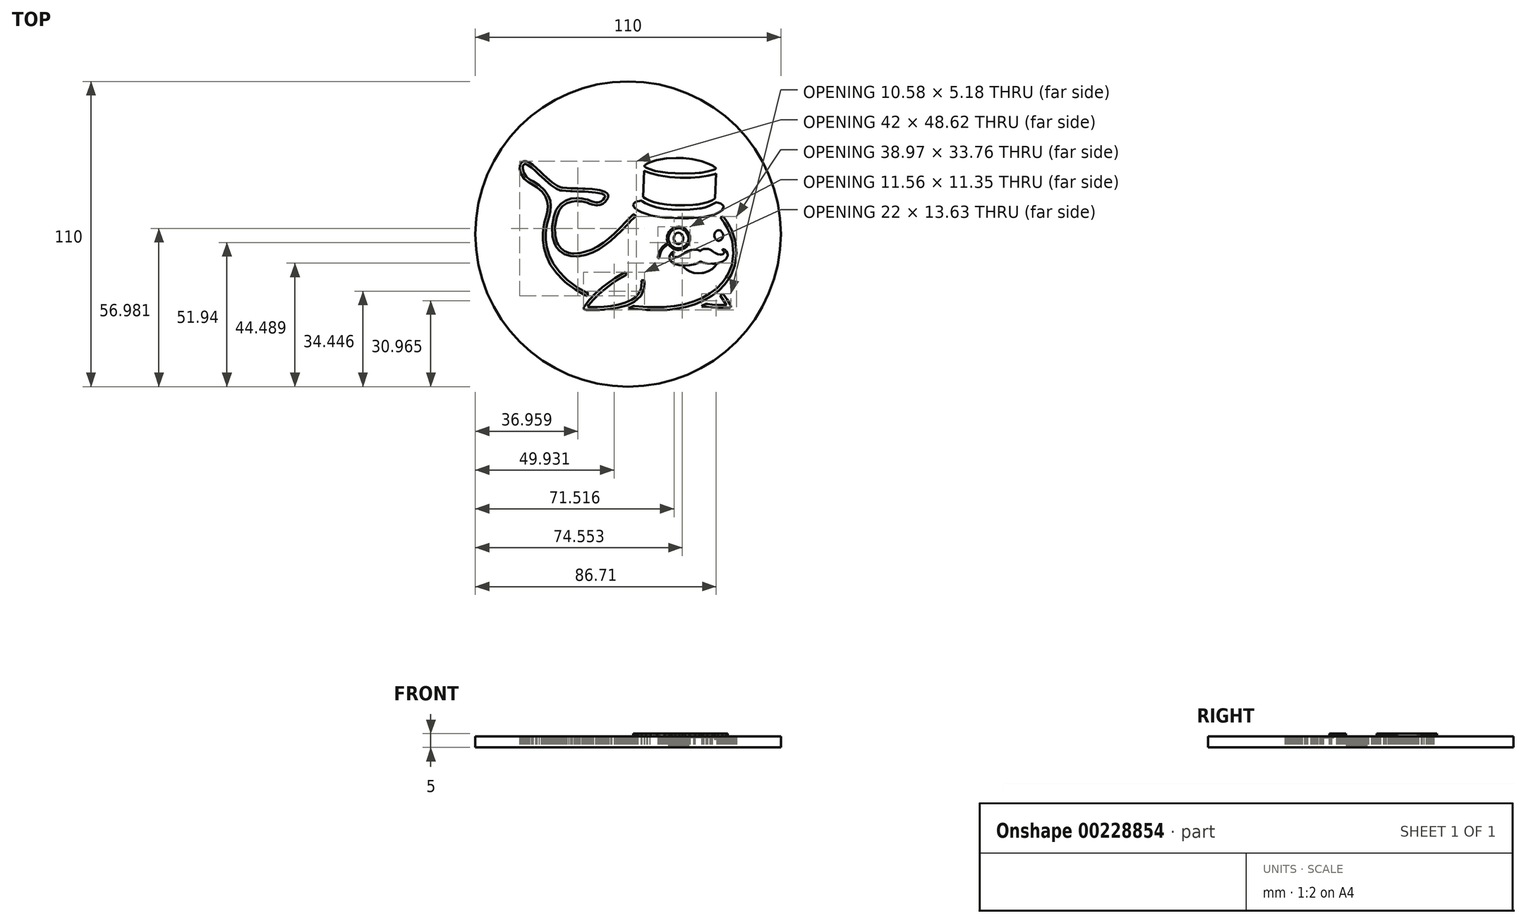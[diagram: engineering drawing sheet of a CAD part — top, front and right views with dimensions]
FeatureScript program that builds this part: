
annotation { "Feature Type Name" : "Feature", "Feature Type Description" : "" }
export const myFeature = defineFeature(function(context is Context, id is Id, definition is map)
    precondition{}
    {
        {
            var Q0;
            Q0=qCreatedBy(makeId("Top.planeOp"),FACE);
            var sketch = newSketch(context, id + "F0", { "sketchPlane" : qUnion([Q0])});
            skLineSegment(sketch, "E0", {"start": v(32.1, -10.6) * mm, "end": v(31.33, -11.62) * mm});
            skLineSegment(sketch, "E1", {"start": v(31.33, -11.62) * mm, "end": v(30.27, -12.6) * mm});
            skLineSegment(sketch, "E2", {"start": v(30.27, -12.6) * mm, "end": v(28.86, -13.41) * mm});
            skLineSegment(sketch, "E3", {"start": v(28.86, -13.41) * mm, "end": v(27.52, -13.88) * mm});
            skLineSegment(sketch, "E4", {"start": v(27.52, -13.88) * mm, "end": v(27.06, -13.97) * mm});
            skLineSegment(sketch, "E5", {"start": v(27.06, -13.97) * mm, "end": v(26.62, -14.05) * mm});
            skLineSegment(sketch, "E6", {"start": v(26.62, -14.05) * mm, "end": v(25.25, -14.14) * mm});
            skLineSegment(sketch, "E7", {"start": v(25.25, -14.14) * mm, "end": v(23.67, -13.98) * mm});
            skLineSegment(sketch, "E8", {"start": v(23.67, -13.98) * mm, "end": v(22.32, -13.55) * mm});
            skLineSegment(sketch, "E9", {"start": v(22.32, -13.55) * mm, "end": v(21.18, -12.9) * mm});
            skLineSegment(sketch, "E10", {"start": v(21.18, -12.9) * mm, "end": v(20.26, -12.09) * mm});
            skLineSegment(sketch, "E11", {"start": v(-13.86, -27.34) * mm, "end": v(-13.89, -27.34) * mm});
            skLineSegment(sketch, "E12", {"start": v(-13.89, -27.34) * mm, "end": v(-14.11, -27.33) * mm});
            skLineSegment(sketch, "E13", {"start": v(-14.11, -27.33) * mm, "end": v(-14.14, -27.33) * mm});
            skLineSegment(sketch, "E14", {"start": v(-14.14, -27.33) * mm, "end": v(-14.36, -27.32) * mm});
            skLineSegment(sketch, "E15", {"start": v(-14.36, -27.32) * mm, "end": v(-15.05, -27.28) * mm});
            skLineSegment(sketch, "E16", {"start": v(-15.05, -27.28) * mm, "end": v(-15.57, -27.22) * mm});
            skLineSegment(sketch, "E17", {"start": v(-15.57, -27.22) * mm, "end": v(-15.82, -27.1) * mm});
            skLineSegment(sketch, "E18", {"start": v(-15.82, -27.1) * mm, "end": v(-15.92, -26.97) * mm});
            skLineSegment(sketch, "E19", {"start": v(-15.92, -26.97) * mm, "end": v(-15.95, -26.92) * mm});
            skLineSegment(sketch, "E20", {"start": v(-15.95, -26.92) * mm, "end": v(-16.07, -26.66) * mm});
            skLineSegment(sketch, "E21", {"start": v(-16.07, -26.66) * mm, "end": v(-15.92, -26.41) * mm});
            skLineSegment(sketch, "E22", {"start": v(-15.92, -26.41) * mm, "end": v(-15.49, -25.72) * mm});
            skLineSegment(sketch, "E23", {"start": v(-15.49, -25.72) * mm, "end": v(-14, -23.78) * mm});
            skLineSegment(sketch, "E24", {"start": v(-14, -23.78) * mm, "end": v(-11.74, -21.38) * mm});
            skLineSegment(sketch, "E25", {"start": v(-11.74, -21.38) * mm, "end": v(-9.33, -19.25) * mm});
            skLineSegment(sketch, "E26", {"start": v(-9.33, -19.25) * mm, "end": v(-6.94, -17.41) * mm});
            skLineSegment(sketch, "E27", {"start": v(-6.94, -17.41) * mm, "end": v(-4.74, -15.91) * mm});
            skLineSegment(sketch, "E28", {"start": v(-4.74, -15.91) * mm, "end": v(-2.9, -14.78) * mm});
            skLineSegment(sketch, "E29", {"start": v(-2.9, -14.78) * mm, "end": v(-1.6, -14.04) * mm});
            skLineSegment(sketch, "E30", {"start": v(-1.6, -14.04) * mm, "end": v(-1.14, -13.8) * mm});
            skLineSegment(sketch, "E31", {"start": v(-1.14, -13.8) * mm, "end": v(-1.03, -13.74) * mm});
            skLineSegment(sketch, "E32", {"start": v(-1.03, -13.74) * mm, "end": v(-0.55, -14.68) * mm});
            skLineSegment(sketch, "E33", {"start": v(-0.55, -14.68) * mm, "end": v(-0.57, -14.7) * mm});
            skLineSegment(sketch, "E34", {"start": v(-0.57, -14.7) * mm, "end": v(-1, -14.92) * mm});
            skLineSegment(sketch, "E35", {"start": v(-1, -14.92) * mm, "end": v(-2.13, -15.57) * mm});
            skLineSegment(sketch, "E36", {"start": v(-2.13, -15.57) * mm, "end": v(-3.81, -16.6) * mm});
            skLineSegment(sketch, "E37", {"start": v(-3.81, -16.6) * mm, "end": v(-5.87, -17.98) * mm});
            skLineSegment(sketch, "E38", {"start": v(-5.87, -17.98) * mm, "end": v(-8.13, -19.67) * mm});
            skLineSegment(sketch, "E39", {"start": v(-8.13, -19.67) * mm, "end": v(-10.44, -21.63) * mm});
            skLineSegment(sketch, "E40", {"start": v(-10.44, -21.63) * mm, "end": v(-12.63, -23.84) * mm});
            skLineSegment(sketch, "E41", {"start": v(-12.63, -23.84) * mm, "end": v(-14.11, -25.62) * mm});
            skLineSegment(sketch, "E42", {"start": v(-14.11, -25.62) * mm, "end": v(-14.54, -26.26) * mm});
            skLineSegment(sketch, "E43", {"start": v(-14.54, -26.26) * mm, "end": v(-14.18, -26.28) * mm});
            skLineSegment(sketch, "E44", {"start": v(-14.18, -26.28) * mm, "end": v(-13.07, -26.3) * mm});
            skLineSegment(sketch, "E45", {"start": v(-13.07, -26.3) * mm, "end": v(-11.07, -26.3) * mm});
            skLineSegment(sketch, "E46", {"start": v(-11.07, -26.3) * mm, "end": v(-8.7, -26.18) * mm});
            skLineSegment(sketch, "E47", {"start": v(-8.7, -26.18) * mm, "end": v(-6.1, -25.9) * mm});
            skLineSegment(sketch, "E48", {"start": v(-6.1, -25.9) * mm, "end": v(-3.47, -25.43) * mm});
            skLineSegment(sketch, "E49", {"start": v(-3.47, -25.43) * mm, "end": v(-0.95, -24.7) * mm});
            skLineSegment(sketch, "E50", {"start": v(-0.95, -24.7) * mm, "end": v(1.31, -23.68) * mm});
            skLineSegment(sketch, "E51", {"start": v(1.31, -23.68) * mm, "end": v(2.74, -22.72) * mm});
            skLineSegment(sketch, "E52", {"start": v(2.74, -22.72) * mm, "end": v(3.14, -22.32) * mm});
            skLineSegment(sketch, "E53", {"start": v(3.14, -22.32) * mm, "end": v(3.51, -21.95) * mm});
            skLineSegment(sketch, "E54", {"start": v(3.51, -21.95) * mm, "end": v(4.66, -19.81) * mm});
            skLineSegment(sketch, "E55", {"start": v(4.66, -19.81) * mm, "end": v(4.85, -17.28) * mm});
            skLineSegment(sketch, "E56", {"start": v(4.85, -17.28) * mm, "end": v(4.75, -16.71) * mm});
            skLineSegment(sketch, "E57", {"start": v(4.75, -16.71) * mm, "end": v(5.8, -16.52) * mm});
            skLineSegment(sketch, "E58", {"start": v(5.8, -16.52) * mm, "end": v(5.93, -17.27) * mm});
            skLineSegment(sketch, "E59", {"start": v(5.93, -17.27) * mm, "end": v(5.8, -19.62) * mm});
            skLineSegment(sketch, "E60", {"start": v(5.8, -19.62) * mm, "end": v(4.6, -22.25) * mm});
            skLineSegment(sketch, "E61", {"start": v(4.6, -22.25) * mm, "end": v(2.24, -24.36) * mm});
            skLineSegment(sketch, "E62", {"start": v(2.24, -24.36) * mm, "end": v(-0.36, -25.65) * mm});
            skLineSegment(sketch, "E63", {"start": v(-0.36, -25.65) * mm, "end": v(-1.27, -25.94) * mm});
            skLineSegment(sketch, "E64", {"start": v(-1.27, -25.94) * mm, "end": v(-1.88, -26.14) * mm});
            skLineSegment(sketch, "E65", {"start": v(-1.88, -26.14) * mm, "end": v(-3.75, -26.58) * mm});
            skLineSegment(sketch, "E66", {"start": v(-3.75, -26.58) * mm, "end": v(-6.24, -27) * mm});
            skLineSegment(sketch, "E67", {"start": v(-6.24, -27) * mm, "end": v(-8.61, -27.24) * mm});
            skLineSegment(sketch, "E68", {"start": v(-8.61, -27.24) * mm, "end": v(-10.17, -27.33) * mm});
            skLineSegment(sketch, "E69", {"start": v(-10.17, -27.33) * mm, "end": v(-10.7, -27.35) * mm});
            skLineSegment(sketch, "E70", {"start": v(-10.7, -27.35) * mm, "end": v(-11.03, -27.36) * mm});
            skLineSegment(sketch, "E71", {"start": v(-11.03, -27.36) * mm, "end": v(-12.5, -27.37) * mm});
            skLineSegment(sketch, "E72", {"start": v(-12.5, -27.37) * mm, "end": v(-13.67, -27.35) * mm});
            skLineSegment(sketch, "E73", {"start": v(-13.67, -27.35) * mm, "end": v(-13.86, -27.34) * mm});
            skLineSegment(sketch, "E74", {"start": v(36.97, -25.78) * mm, "end": v(36.76, -25.4) * mm});
            skLineSegment(sketch, "E75", {"start": v(36.76, -25.4) * mm, "end": v(35.57, -23.58) * mm});
            skLineSegment(sketch, "E76", {"start": v(35.57, -23.58) * mm, "end": v(34.3, -21.79) * mm});
            skLineSegment(sketch, "E77", {"start": v(34.3, -21.79) * mm, "end": v(34.04, -21.45) * mm});
            skLineSegment(sketch, "E78", {"start": v(34.04, -21.45) * mm, "end": v(33.97, -21.5) * mm});
            skLineSegment(sketch, "E79", {"start": v(33.97, -21.5) * mm, "end": v(33.21, -22.11) * mm});
            skLineSegment(sketch, "E80", {"start": v(33.21, -22.11) * mm, "end": v(33.14, -22.17) * mm});
            skLineSegment(sketch, "E81", {"start": v(33.14, -22.17) * mm, "end": v(33.34, -22.44) * mm});
            skLineSegment(sketch, "E82", {"start": v(33.34, -22.44) * mm, "end": v(35.28, -25.25) * mm});
            skLineSegment(sketch, "E83", {"start": v(35.28, -25.25) * mm, "end": v(35.46, -25.54) * mm});
            skLineSegment(sketch, "E84", {"start": v(35.46, -25.54) * mm, "end": v(35.11, -25.55) * mm});
            skLineSegment(sketch, "E85", {"start": v(35.11, -25.55) * mm, "end": v(34.08, -25.57) * mm});
            skLineSegment(sketch, "E86", {"start": v(34.08, -25.57) * mm, "end": v(32.29, -25.53) * mm});
            skLineSegment(sketch, "E87", {"start": v(32.29, -25.53) * mm, "end": v(30.24, -25.4) * mm});
            skLineSegment(sketch, "E88", {"start": v(30.24, -25.4) * mm, "end": v(28.63, -25.22) * mm});
            skLineSegment(sketch, "E89", {"start": v(28.63, -25.22) * mm, "end": v(28.1, -25.13) * mm});
            skLineSegment(sketch, "E90", {"start": v(28.1, -25.13) * mm, "end": v(27.95, -25.2) * mm});
            skLineSegment(sketch, "E91", {"start": v(27.95, -25.2) * mm, "end": v(26.55, -25.84) * mm});
            skLineSegment(sketch, "E92", {"start": v(26.55, -25.84) * mm, "end": v(26.42, -25.9) * mm});
            skLineSegment(sketch, "E93", {"start": v(26.42, -25.9) * mm, "end": v(26.72, -25.96) * mm});
            skLineSegment(sketch, "E94", {"start": v(26.72, -25.96) * mm, "end": v(29.78, -26.42) * mm});
            skLineSegment(sketch, "E95", {"start": v(29.78, -26.42) * mm, "end": v(30.07, -26.45) * mm});
            skLineSegment(sketch, "E96", {"start": v(30.07, -26.45) * mm, "end": v(30.26, -26.47) * mm});
            skLineSegment(sketch, "E97", {"start": v(30.26, -26.47) * mm, "end": v(32.03, -26.58) * mm});
            skLineSegment(sketch, "E98", {"start": v(32.03, -26.58) * mm, "end": v(32.19, -26.59) * mm});
            skLineSegment(sketch, "E99", {"start": v(32.19, -26.59) * mm, "end": v(32.51, -26.6) * mm});
            skLineSegment(sketch, "E100", {"start": v(32.51, -26.6) * mm, "end": v(33.94, -26.62) * mm});
            skLineSegment(sketch, "E101", {"start": v(33.94, -26.62) * mm, "end": v(35.07, -26.61) * mm});
            skLineSegment(sketch, "E102", {"start": v(35.07, -26.61) * mm, "end": v(35.24, -26.6) * mm});
            skLineSegment(sketch, "E103", {"start": v(35.24, -26.6) * mm, "end": v(35.45, -26.6) * mm});
            skLineSegment(sketch, "E104", {"start": v(35.45, -26.6) * mm, "end": v(36.07, -26.58) * mm});
            skLineSegment(sketch, "E105", {"start": v(36.07, -26.58) * mm, "end": v(36.55, -26.53) * mm});
            skLineSegment(sketch, "E106", {"start": v(36.55, -26.53) * mm, "end": v(36.81, -26.44) * mm});
            skLineSegment(sketch, "E107", {"start": v(36.81, -26.44) * mm, "end": v(36.93, -26.33) * mm});
            skLineSegment(sketch, "E108", {"start": v(36.93, -26.33) * mm, "end": v(36.96, -26.28) * mm});
            skLineSegment(sketch, "E109", {"start": v(36.96, -26.28) * mm, "end": v(36.99, -26.24) * mm});
            skLineSegment(sketch, "E110", {"start": v(36.99, -26.24) * mm, "end": v(37, -25.82) * mm});
            skLineSegment(sketch, "E111", {"start": v(37, -25.82) * mm, "end": v(36.97, -25.78) * mm});
            skLineSegment(sketch, "E112", {"start": v(2.96, 6.57) * mm, "end": v(2.86, 6.61) * mm});
            skLineSegment(sketch, "E113", {"start": v(2.86, 6.61) * mm, "end": v(1.97, 7.02) * mm});
            skLineSegment(sketch, "E114", {"start": v(1.97, 7.02) * mm, "end": v(1.89, 7.06) * mm});
            skLineSegment(sketch, "E115", {"start": v(1.89, 7.06) * mm, "end": v(1.65, 6.85) * mm});
            skLineSegment(sketch, "E116", {"start": v(1.65, 6.85) * mm, "end": v(0.96, 6.21) * mm});
            skLineSegment(sketch, "E117", {"start": v(0.96, 6.21) * mm, "end": v(0.2, 5.45) * mm});
            skLineSegment(sketch, "E118", {"start": v(0.2, 5.45) * mm, "end": v(-0.57, 4.63) * mm});
            skLineSegment(sketch, "E119", {"start": v(-0.57, 4.63) * mm, "end": v(-1.3, 3.87) * mm});
            skLineSegment(sketch, "E120", {"start": v(-1.3, 3.87) * mm, "end": v(-1.53, 3.62) * mm});
            skLineSegment(sketch, "E121", {"start": v(-1.53, 3.62) * mm, "end": v(-1.95, 3.19) * mm});
            skLineSegment(sketch, "E122", {"start": v(-1.95, 3.19) * mm, "end": v(-3.23, 1.88) * mm});
            skLineSegment(sketch, "E123", {"start": v(-3.23, 1.88) * mm, "end": v(-5, 0.14) * mm});
            skLineSegment(sketch, "E124", {"start": v(-5, 0.14) * mm, "end": v(-6.86, -1.54) * mm});
            skLineSegment(sketch, "E125", {"start": v(-6.86, -1.54) * mm, "end": v(-8.83, -3.1) * mm});
            skLineSegment(sketch, "E126", {"start": v(-8.83, -3.1) * mm, "end": v(-10.92, -4.48) * mm});
            skLineSegment(sketch, "E127", {"start": v(-10.92, -4.48) * mm, "end": v(-13.15, -5.62) * mm});
            skLineSegment(sketch, "E128", {"start": v(-13.15, -5.62) * mm, "end": v(-15.54, -6.45) * mm});
            skLineSegment(sketch, "E129", {"start": v(-15.54, -6.45) * mm, "end": v(-17.46, -6.86) * mm});
            skLineSegment(sketch, "E130", {"start": v(-17.46, -6.86) * mm, "end": v(-18.1, -6.93) * mm});
            skLineSegment(sketch, "E131", {"start": v(-18.1, -6.93) * mm, "end": v(-18.24, -6.94) * mm});
            skLineSegment(sketch, "E132", {"start": v(-18.24, -6.94) * mm, "end": v(-19.5, -6.99) * mm});
            skLineSegment(sketch, "E133", {"start": v(-19.5, -6.99) * mm, "end": v(-19.62, -6.98) * mm});
            skLineSegment(sketch, "E134", {"start": v(-19.62, -6.98) * mm, "end": v(-20.07, -6.97) * mm});
            skLineSegment(sketch, "E135", {"start": v(-20.07, -6.97) * mm, "end": v(-21.4, -6.72) * mm});
            skLineSegment(sketch, "E136", {"start": v(-21.4, -6.72) * mm, "end": v(-22.93, -6.1) * mm});
            skLineSegment(sketch, "E137", {"start": v(-22.93, -6.1) * mm, "end": v(-24.19, -5.1) * mm});
            skLineSegment(sketch, "E138", {"start": v(-24.19, -5.1) * mm, "end": v(-24.98, -4.1) * mm});
            skLineSegment(sketch, "E139", {"start": v(-24.98, -4.1) * mm, "end": v(-25.18, -3.73) * mm});
            skLineSegment(sketch, "E140", {"start": v(-25.18, -3.73) * mm, "end": v(-25.55, -3.05) * mm});
            skLineSegment(sketch, "E141", {"start": v(-25.55, -3.05) * mm, "end": v(-26.17, -0.73) * mm});
            skLineSegment(sketch, "E142", {"start": v(-26.17, -0.73) * mm, "end": v(-26.31, 2.66) * mm});
            skLineSegment(sketch, "E143", {"start": v(-26.31, 2.66) * mm, "end": v(-25.74, 5.98) * mm});
            skLineSegment(sketch, "E144", {"start": v(-25.74, 5.98) * mm, "end": v(-24.97, 8.14) * mm});
            skLineSegment(sketch, "E145", {"start": v(-24.97, 8.14) * mm, "end": v(-24.6, 8.79) * mm});
            skLineSegment(sketch, "E146", {"start": v(-24.6, 8.79) * mm, "end": v(-24.37, 9.17) * mm});
            skLineSegment(sketch, "E147", {"start": v(-24.37, 9.17) * mm, "end": v(-23.49, 10.18) * mm});
            skLineSegment(sketch, "E148", {"start": v(-23.49, 10.18) * mm, "end": v(-22.03, 11.15) * mm});
            skLineSegment(sketch, "E149", {"start": v(-22.03, 11.15) * mm, "end": v(-20.22, 11.7) * mm});
            skLineSegment(sketch, "E150", {"start": v(-20.22, 11.7) * mm, "end": v(-18.6, 11.85) * mm});
            skLineSegment(sketch, "E151", {"start": v(-18.6, 11.85) * mm, "end": v(-18.07, 11.83) * mm});
            skLineSegment(sketch, "E152", {"start": v(-18.07, 11.83) * mm, "end": v(-17.73, 11.82) * mm});
            skLineSegment(sketch, "E153", {"start": v(-17.73, 11.82) * mm, "end": v(-16.72, 11.7) * mm});
            skLineSegment(sketch, "E154", {"start": v(-16.72, 11.7) * mm, "end": v(-15.61, 11.51) * mm});
            skLineSegment(sketch, "E155", {"start": v(-15.61, 11.51) * mm, "end": v(-14.87, 11.33) * mm});
            skLineSegment(sketch, "E156", {"start": v(-14.87, 11.33) * mm, "end": v(-14.66, 11.24) * mm});
            skLineSegment(sketch, "E157", {"start": v(-14.66, 11.24) * mm, "end": v(-14.6, 11.24) * mm});
            skLineSegment(sketch, "E158", {"start": v(-14.6, 11.24) * mm, "end": v(-14.33, 11.15) * mm});
            skLineSegment(sketch, "E159", {"start": v(-14.33, 11.15) * mm, "end": v(-14.1, 11.06) * mm});
            skLineSegment(sketch, "E160", {"start": v(-14.1, 11.06) * mm, "end": v(-12.86, 10.63) * mm});
            skLineSegment(sketch, "E161", {"start": v(-12.86, 10.63) * mm, "end": v(-11.55, 10.36) * mm});
            skLineSegment(sketch, "E162", {"start": v(-11.55, 10.36) * mm, "end": v(-11.28, 10.35) * mm});
            skLineSegment(sketch, "E163", {"start": v(-11.28, 10.35) * mm, "end": v(-11, 10.34) * mm});
            skLineSegment(sketch, "E164", {"start": v(-11, 10.34) * mm, "end": v(-10.15, 10.46) * mm});
            skLineSegment(sketch, "E165", {"start": v(-10.15, 10.46) * mm, "end": v(-9.14, 10.88) * mm});
            skLineSegment(sketch, "E166", {"start": v(-9.14, 10.88) * mm, "end": v(-8.25, 11.6) * mm});
            skLineSegment(sketch, "E167", {"start": v(-8.25, 11.6) * mm, "end": v(-7.64, 12.38) * mm});
            skLineSegment(sketch, "E168", {"start": v(-7.64, 12.38) * mm, "end": v(-7.47, 12.66) * mm});
            skLineSegment(sketch, "E169", {"start": v(-7.47, 12.66) * mm, "end": v(-7.4, 12.78) * mm});
            skLineSegment(sketch, "E170", {"start": v(-7.4, 12.78) * mm, "end": v(-7.23, 13.2) * mm});
            skLineSegment(sketch, "E171", {"start": v(-7.23, 13.2) * mm, "end": v(-7.16, 13.67) * mm});
            skLineSegment(sketch, "E172", {"start": v(-7.16, 13.67) * mm, "end": v(-7.21, 14.05) * mm});
            skLineSegment(sketch, "E173", {"start": v(-7.21, 14.05) * mm, "end": v(-7.3, 14.29) * mm});
            skLineSegment(sketch, "E174", {"start": v(-7.3, 14.29) * mm, "end": v(-7.33, 14.36) * mm});
            skLineSegment(sketch, "E175", {"start": v(-7.33, 14.36) * mm, "end": v(-7.49, 14.64) * mm});
            skLineSegment(sketch, "E176", {"start": v(-7.49, 14.64) * mm, "end": v(-8.36, 15.25) * mm});
            skLineSegment(sketch, "E177", {"start": v(-8.36, 15.25) * mm, "end": v(-10.22, 15.82) * mm});
            skLineSegment(sketch, "E178", {"start": v(-10.22, 15.82) * mm, "end": v(-12.86, 16.17) * mm});
            skLineSegment(sketch, "E179", {"start": v(-12.86, 16.17) * mm, "end": v(-15.36, 16.32) * mm});
            skLineSegment(sketch, "E180", {"start": v(-15.36, 16.32) * mm, "end": v(-16.2, 16.35) * mm});
            skLineSegment(sketch, "E181", {"start": v(-16.2, 16.35) * mm, "end": v(-16.38, 16.36) * mm});
            skLineSegment(sketch, "E182", {"start": v(-16.38, 16.36) * mm, "end": v(-18.12, 16.42) * mm});
            skLineSegment(sketch, "E183", {"start": v(-18.12, 16.42) * mm, "end": v(-18.29, 16.42) * mm});
            skLineSegment(sketch, "E184", {"start": v(-18.29, 16.42) * mm, "end": v(-18.45, 16.43) * mm});
            skLineSegment(sketch, "E185", {"start": v(-18.45, 16.43) * mm, "end": v(-20.07, 16.48) * mm});
            skLineSegment(sketch, "E186", {"start": v(-20.07, 16.48) * mm, "end": v(-20.22, 16.48) * mm});
            skLineSegment(sketch, "E187", {"start": v(-20.22, 16.48) * mm, "end": v(-20.5, 16.5) * mm});
            skLineSegment(sketch, "E188", {"start": v(-20.5, 16.5) * mm, "end": v(-22.06, 16.57) * mm});
            skLineSegment(sketch, "E189", {"start": v(-22.06, 16.57) * mm, "end": v(-23.57, 16.7) * mm});
            skLineSegment(sketch, "E190", {"start": v(-23.57, 16.7) * mm, "end": v(-23.82, 16.74) * mm});
            skLineSegment(sketch, "E191", {"start": v(-23.82, 16.74) * mm, "end": v(-24.25, 16.8) * mm});
            skLineSegment(sketch, "E192", {"start": v(-24.25, 16.8) * mm, "end": v(-25.5, 17.35) * mm});
            skLineSegment(sketch, "E193", {"start": v(-25.5, 17.35) * mm, "end": v(-27.32, 18.6) * mm});
            skLineSegment(sketch, "E194", {"start": v(-27.32, 18.6) * mm, "end": v(-29.21, 20.23) * mm});
            skLineSegment(sketch, "E195", {"start": v(-29.21, 20.23) * mm, "end": v(-30.62, 21.55) * mm});
            skLineSegment(sketch, "E196", {"start": v(-30.62, 21.55) * mm, "end": v(-31.08, 22) * mm});
            skLineSegment(sketch, "E197", {"start": v(-31.08, 22) * mm, "end": v(-31.5, 22.4) * mm});
            skLineSegment(sketch, "E198", {"start": v(-31.5, 22.4) * mm, "end": v(-32.8, 23.61) * mm});
            skLineSegment(sketch, "E199", {"start": v(-32.8, 23.61) * mm, "end": v(-34.38, 24.97) * mm});
            skLineSegment(sketch, "E200", {"start": v(-34.38, 24.97) * mm, "end": v(-35.8, 25.91) * mm});
            skLineSegment(sketch, "E201", {"start": v(-35.8, 25.91) * mm, "end": v(-36.74, 26.28) * mm});
            skLineSegment(sketch, "E202", {"start": v(-36.74, 26.28) * mm, "end": v(-37.06, 26.29) * mm});
            skLineSegment(sketch, "E203", {"start": v(-37.06, 26.29) * mm, "end": v(-37.16, 26.3) * mm});
            skLineSegment(sketch, "E204", {"start": v(-37.16, 26.3) * mm, "end": v(-37.48, 26.25) * mm});
            skLineSegment(sketch, "E205", {"start": v(-37.48, 26.25) * mm, "end": v(-37.94, 26.08) * mm});
            skLineSegment(sketch, "E206", {"start": v(-37.94, 26.08) * mm, "end": v(-38.38, 25.73) * mm});
            skLineSegment(sketch, "E207", {"start": v(-38.38, 25.73) * mm, "end": v(-38.69, 25.28) * mm});
            skLineSegment(sketch, "E208", {"start": v(-38.69, 25.28) * mm, "end": v(-38.76, 25.12) * mm});
            skLineSegment(sketch, "E209", {"start": v(-38.76, 25.12) * mm, "end": v(-38.92, 24.76) * mm});
            skLineSegment(sketch, "E210", {"start": v(-38.92, 24.76) * mm, "end": v(-39.04, 23.5) * mm});
            skLineSegment(sketch, "E211", {"start": v(-39.04, 23.5) * mm, "end": v(-38.6, 21.7) * mm});
            skLineSegment(sketch, "E212", {"start": v(-38.6, 21.7) * mm, "end": v(-37.42, 19.93) * mm});
            skLineSegment(sketch, "E213", {"start": v(-37.42, 19.93) * mm, "end": v(-36.04, 18.76) * mm});
            skLineSegment(sketch, "E214", {"start": v(-36.04, 18.76) * mm, "end": v(-35.52, 18.48) * mm});
            skLineSegment(sketch, "E215", {"start": v(-35.52, 18.48) * mm, "end": v(-34.83, 18.1) * mm});
            skLineSegment(sketch, "E216", {"start": v(-34.83, 18.1) * mm, "end": v(-32.85, 16.81) * mm});
            skLineSegment(sketch, "E217", {"start": v(-32.85, 16.81) * mm, "end": v(-30.96, 15.15) * mm});
            skLineSegment(sketch, "E218", {"start": v(-30.96, 15.15) * mm, "end": v(-29.75, 13.49) * mm});
            skLineSegment(sketch, "E219", {"start": v(-29.75, 13.49) * mm, "end": v(-29.1, 11.81) * mm});
            skLineSegment(sketch, "E220", {"start": v(-29.1, 11.81) * mm, "end": v(-28.88, 10.14) * mm});
            skLineSegment(sketch, "E221", {"start": v(-28.88, 10.14) * mm, "end": v(-29.02, 8.44) * mm});
            skLineSegment(sketch, "E222", {"start": v(-29.02, 8.44) * mm, "end": v(-29.38, 6.73) * mm});
            skLineSegment(sketch, "E223", {"start": v(-29.38, 6.73) * mm, "end": v(-29.73, 5.44) * mm});
            skLineSegment(sketch, "E224", {"start": v(-29.73, 5.44) * mm, "end": v(-29.85, 5) * mm});
            skLineSegment(sketch, "E225", {"start": v(-29.85, 5) * mm, "end": v(-29.98, 4.58) * mm});
            skLineSegment(sketch, "E226", {"start": v(-29.98, 4.58) * mm, "end": v(-30.11, 4.1) * mm});
            skLineSegment(sketch, "E227", {"start": v(-30.11, 4.1) * mm, "end": v(-30.43, 2.65) * mm});
            skLineSegment(sketch, "E228", {"start": v(-30.43, 2.65) * mm, "end": v(-30.71, 0.37) * mm});
            skLineSegment(sketch, "E229", {"start": v(-30.71, 0.37) * mm, "end": v(-30.72, -2.2) * mm});
            skLineSegment(sketch, "E230", {"start": v(-30.72, -2.2) * mm, "end": v(-30.34, -5) * mm});
            skLineSegment(sketch, "E231", {"start": v(-30.34, -5) * mm, "end": v(-29.46, -7.96) * mm});
            skLineSegment(sketch, "E232", {"start": v(-29.46, -7.96) * mm, "end": v(-27.95, -11.04) * mm});
            skLineSegment(sketch, "E233", {"start": v(-27.95, -11.04) * mm, "end": v(-25.7, -14.17) * mm});
            skLineSegment(sketch, "E234", {"start": v(-25.7, -14.17) * mm, "end": v(-23.44, -16.57) * mm});
            skLineSegment(sketch, "E235", {"start": v(-23.44, -16.57) * mm, "end": v(-22.62, -17.3) * mm});
            skLineSegment(sketch, "E236", {"start": v(-22.62, -17.3) * mm, "end": v(-22.06, -17.78) * mm});
            skLineSegment(sketch, "E237", {"start": v(-22.06, -17.78) * mm, "end": v(-19, -20) * mm});
            skLineSegment(sketch, "E238", {"start": v(-19, -20) * mm, "end": v(-15.6, -21.98) * mm});
            skLineSegment(sketch, "E239", {"start": v(-15.6, -21.98) * mm, "end": v(-14.86, -22.33) * mm});
            skLineSegment(sketch, "E240", {"start": v(-14.86, -22.33) * mm, "end": v(-14.81, -22.26) * mm});
            skLineSegment(sketch, "E241", {"start": v(-14.81, -22.26) * mm, "end": v(-14.3, -21.53) * mm});
            skLineSegment(sketch, "E242", {"start": v(-14.3, -21.53) * mm, "end": v(-14.23, -21.45) * mm});
            skLineSegment(sketch, "E243", {"start": v(-14.23, -21.45) * mm, "end": v(-14.96, -21.1) * mm});
            skLineSegment(sketch, "E244", {"start": v(-14.96, -21.1) * mm, "end": v(-18.34, -19.17) * mm});
            skLineSegment(sketch, "E245", {"start": v(-18.34, -19.17) * mm, "end": v(-21.37, -16.97) * mm});
            skLineSegment(sketch, "E246", {"start": v(-21.37, -16.97) * mm, "end": v(-21.92, -16.49) * mm});
            skLineSegment(sketch, "E247", {"start": v(-21.92, -16.49) * mm, "end": v(-22.7, -15.8) * mm});
            skLineSegment(sketch, "E248", {"start": v(-22.7, -15.8) * mm, "end": v(-24.86, -13.51) * mm});
            skLineSegment(sketch, "E249", {"start": v(-24.86, -13.51) * mm, "end": v(-27, -10.54) * mm});
            skLineSegment(sketch, "E250", {"start": v(-27, -10.54) * mm, "end": v(-28.44, -7.6) * mm});
            skLineSegment(sketch, "E251", {"start": v(-28.44, -7.6) * mm, "end": v(-29.29, -4.8) * mm});
            skLineSegment(sketch, "E252", {"start": v(-29.29, -4.8) * mm, "end": v(-29.66, -2.13) * mm});
            skLineSegment(sketch, "E253", {"start": v(-29.66, -2.13) * mm, "end": v(-29.65, 0.3) * mm});
            skLineSegment(sketch, "E254", {"start": v(-29.65, 0.3) * mm, "end": v(-29.38, 2.46) * mm});
            skLineSegment(sketch, "E255", {"start": v(-29.38, 2.46) * mm, "end": v(-29.08, 3.84) * mm});
            skLineSegment(sketch, "E256", {"start": v(-29.08, 3.84) * mm, "end": v(-28.95, 4.29) * mm});
            skLineSegment(sketch, "E257", {"start": v(-28.95, 4.29) * mm, "end": v(-28.83, 4.71) * mm});
            skLineSegment(sketch, "E258", {"start": v(-28.83, 4.71) * mm, "end": v(-28.7, 5.15) * mm});
            skLineSegment(sketch, "E259", {"start": v(-28.7, 5.15) * mm, "end": v(-28.35, 6.47) * mm});
            skLineSegment(sketch, "E260", {"start": v(-28.35, 6.47) * mm, "end": v(-27.97, 8.27) * mm});
            skLineSegment(sketch, "E261", {"start": v(-27.97, 8.27) * mm, "end": v(-27.83, 10.11) * mm});
            skLineSegment(sketch, "E262", {"start": v(-27.83, 10.11) * mm, "end": v(-28.05, 11.98) * mm});
            skLineSegment(sketch, "E263", {"start": v(-28.05, 11.98) * mm, "end": v(-28.75, 13.85) * mm});
            skLineSegment(sketch, "E264", {"start": v(-28.75, 13.85) * mm, "end": v(-30.06, 15.72) * mm});
            skLineSegment(sketch, "E265", {"start": v(-30.06, 15.72) * mm, "end": v(-32.1, 17.58) * mm});
            skLineSegment(sketch, "E266", {"start": v(-32.1, 17.58) * mm, "end": v(-34.26, 19) * mm});
            skLineSegment(sketch, "E267", {"start": v(-34.26, 19) * mm, "end": v(-35.02, 19.41) * mm});
            skLineSegment(sketch, "E268", {"start": v(-35.02, 19.41) * mm, "end": v(-35.46, 19.65) * mm});
            skLineSegment(sketch, "E269", {"start": v(-35.46, 19.65) * mm, "end": v(-36.62, 20.64) * mm});
            skLineSegment(sketch, "E270", {"start": v(-36.62, 20.64) * mm, "end": v(-37.58, 22.1) * mm});
            skLineSegment(sketch, "E271", {"start": v(-37.58, 22.1) * mm, "end": v(-37.96, 23.52) * mm});
            skLineSegment(sketch, "E272", {"start": v(-37.96, 23.52) * mm, "end": v(-37.9, 24.42) * mm});
            skLineSegment(sketch, "E273", {"start": v(-37.9, 24.42) * mm, "end": v(-37.8, 24.68) * mm});
            skLineSegment(sketch, "E274", {"start": v(-37.8, 24.68) * mm, "end": v(-37.74, 24.8) * mm});
            skLineSegment(sketch, "E275", {"start": v(-37.74, 24.8) * mm, "end": v(-37.44, 25.14) * mm});
            skLineSegment(sketch, "E276", {"start": v(-37.44, 25.14) * mm, "end": v(-37.15, 25.22) * mm});
            skLineSegment(sketch, "E277", {"start": v(-37.15, 25.22) * mm, "end": v(-37.1, 25.22) * mm});
            skLineSegment(sketch, "E278", {"start": v(-37.1, 25.22) * mm, "end": v(-36.84, 25.21) * mm});
            skLineSegment(sketch, "E279", {"start": v(-36.84, 25.21) * mm, "end": v(-36.07, 24.85) * mm});
            skLineSegment(sketch, "E280", {"start": v(-36.07, 24.85) * mm, "end": v(-34.79, 23.94) * mm});
            skLineSegment(sketch, "E281", {"start": v(-34.79, 23.94) * mm, "end": v(-33.34, 22.66) * mm});
            skLineSegment(sketch, "E282", {"start": v(-33.34, 22.66) * mm, "end": v(-32.2, 21.59) * mm});
            skLineSegment(sketch, "E283", {"start": v(-32.2, 21.59) * mm, "end": v(-31.82, 21.22) * mm});
            skLineSegment(sketch, "E284", {"start": v(-31.82, 21.22) * mm, "end": v(-31.32, 20.75) * mm});
            skLineSegment(sketch, "E285", {"start": v(-31.32, 20.75) * mm, "end": v(-29.8, 19.33) * mm});
            skLineSegment(sketch, "E286", {"start": v(-29.8, 19.33) * mm, "end": v(-27.8, 17.62) * mm});
            skLineSegment(sketch, "E287", {"start": v(-27.8, 17.62) * mm, "end": v(-25.84, 16.33) * mm});
            skLineSegment(sketch, "E288", {"start": v(-25.84, 16.33) * mm, "end": v(-24.46, 15.75) * mm});
            skLineSegment(sketch, "E289", {"start": v(-24.46, 15.75) * mm, "end": v(-23.97, 15.68) * mm});
            skLineSegment(sketch, "E290", {"start": v(-23.97, 15.68) * mm, "end": v(-23.76, 15.65) * mm});
            skLineSegment(sketch, "E291", {"start": v(-23.76, 15.65) * mm, "end": v(-22.45, 15.53) * mm});
            skLineSegment(sketch, "E292", {"start": v(-22.45, 15.53) * mm, "end": v(-20.7, 15.43) * mm});
            skLineSegment(sketch, "E293", {"start": v(-20.7, 15.43) * mm, "end": v(-20.26, 15.42) * mm});
            skLineSegment(sketch, "E294", {"start": v(-20.26, 15.42) * mm, "end": v(-20.1, 15.41) * mm});
            skLineSegment(sketch, "E295", {"start": v(-20.1, 15.41) * mm, "end": v(-18.49, 15.36) * mm});
            skLineSegment(sketch, "E296", {"start": v(-18.49, 15.36) * mm, "end": v(-18.32, 15.36) * mm});
            skLineSegment(sketch, "E297", {"start": v(-18.32, 15.36) * mm, "end": v(-18.15, 15.35) * mm});
            skLineSegment(sketch, "E298", {"start": v(-18.15, 15.35) * mm, "end": v(-16.41, 15.3) * mm});
            skLineSegment(sketch, "E299", {"start": v(-16.41, 15.3) * mm, "end": v(-16.24, 15.29) * mm});
            skLineSegment(sketch, "E300", {"start": v(-16.24, 15.29) * mm, "end": v(-15.74, 15.27) * mm});
            skLineSegment(sketch, "E301", {"start": v(-15.74, 15.27) * mm, "end": v(-14.24, 15.2) * mm});
            skLineSegment(sketch, "E302", {"start": v(-14.24, 15.2) * mm, "end": v(-11.74, 14.98) * mm});
            skLineSegment(sketch, "E303", {"start": v(-11.74, 14.98) * mm, "end": v(-9.5, 14.56) * mm});
            skLineSegment(sketch, "E304", {"start": v(-9.5, 14.56) * mm, "end": v(-8.42, 14.12) * mm});
            skLineSegment(sketch, "E305", {"start": v(-8.42, 14.12) * mm, "end": v(-8.27, 13.85) * mm});
            skLineSegment(sketch, "E306", {"start": v(-8.27, 13.85) * mm, "end": v(-8.26, 13.84) * mm});
            skLineSegment(sketch, "E307", {"start": v(-8.26, 13.84) * mm, "end": v(-8.22, 13.66) * mm});
            skLineSegment(sketch, "E308", {"start": v(-8.22, 13.66) * mm, "end": v(-8.33, 13.3) * mm});
            skLineSegment(sketch, "E309", {"start": v(-8.33, 13.3) * mm, "end": v(-8.39, 13.2) * mm});
            skLineSegment(sketch, "E310", {"start": v(-8.39, 13.2) * mm, "end": v(-8.52, 12.99) * mm});
            skLineSegment(sketch, "E311", {"start": v(-8.52, 12.99) * mm, "end": v(-8.99, 12.38) * mm});
            skLineSegment(sketch, "E312", {"start": v(-8.99, 12.38) * mm, "end": v(-9.65, 11.82) * mm});
            skLineSegment(sketch, "E313", {"start": v(-9.65, 11.82) * mm, "end": v(-10.4, 11.5) * mm});
            skLineSegment(sketch, "E314", {"start": v(-10.4, 11.5) * mm, "end": v(-11.03, 11.4) * mm});
            skLineSegment(sketch, "E315", {"start": v(-11.03, 11.4) * mm, "end": v(-11.24, 11.41) * mm});
            skLineSegment(sketch, "E316", {"start": v(-11.24, 11.41) * mm, "end": v(-11.47, 11.42) * mm});
            skLineSegment(sketch, "E317", {"start": v(-11.47, 11.42) * mm, "end": v(-12.6, 11.66) * mm});
            skLineSegment(sketch, "E318", {"start": v(-12.6, 11.66) * mm, "end": v(-13.73, 12.05) * mm});
            skLineSegment(sketch, "E319", {"start": v(-13.73, 12.05) * mm, "end": v(-13.95, 12.14) * mm});
            skLineSegment(sketch, "E320", {"start": v(-13.95, 12.14) * mm, "end": v(-14.23, 12.25) * mm});
            skLineSegment(sketch, "E321", {"start": v(-14.23, 12.25) * mm, "end": v(-14.25, 12.25) * mm});
            skLineSegment(sketch, "E322", {"start": v(-14.25, 12.25) * mm, "end": v(-14.56, 12.35) * mm});
            skLineSegment(sketch, "E323", {"start": v(-14.56, 12.35) * mm, "end": v(-15.38, 12.55) * mm});
            skLineSegment(sketch, "E324", {"start": v(-15.38, 12.55) * mm, "end": v(-16.57, 12.76) * mm});
            skLineSegment(sketch, "E325", {"start": v(-16.57, 12.76) * mm, "end": v(-17.67, 12.88) * mm});
            skLineSegment(sketch, "E326", {"start": v(-17.67, 12.88) * mm, "end": v(-18.03, 12.9) * mm});
            skLineSegment(sketch, "E327", {"start": v(-18.03, 12.9) * mm, "end": v(-18.64, 12.92) * mm});
            skLineSegment(sketch, "E328", {"start": v(-18.64, 12.92) * mm, "end": v(-20.46, 12.73) * mm});
            skLineSegment(sketch, "E329", {"start": v(-20.46, 12.73) * mm, "end": v(-22.54, 12.08) * mm});
            skLineSegment(sketch, "E330", {"start": v(-22.54, 12.08) * mm, "end": v(-24.23, 10.94) * mm});
            skLineSegment(sketch, "E331", {"start": v(-24.23, 10.94) * mm, "end": v(-25.26, 9.76) * mm});
            skLineSegment(sketch, "E332", {"start": v(-25.26, 9.76) * mm, "end": v(-25.51, 9.32) * mm});
            skLineSegment(sketch, "E333", {"start": v(-25.51, 9.32) * mm, "end": v(-25.92, 8.63) * mm});
            skLineSegment(sketch, "E334", {"start": v(-25.92, 8.63) * mm, "end": v(-26.76, 6.32) * mm});
            skLineSegment(sketch, "E335", {"start": v(-26.76, 6.32) * mm, "end": v(-27.38, 2.74) * mm});
            skLineSegment(sketch, "E336", {"start": v(-27.38, 2.74) * mm, "end": v(-27.22, -0.93) * mm});
            skLineSegment(sketch, "E337", {"start": v(-27.22, -0.93) * mm, "end": v(-26.53, -3.49) * mm});
            skLineSegment(sketch, "E338", {"start": v(-26.53, -3.49) * mm, "end": v(-26.11, -4.24) * mm});
            skLineSegment(sketch, "E339", {"start": v(-26.11, -4.24) * mm, "end": v(-25.84, -4.74) * mm});
            skLineSegment(sketch, "E340", {"start": v(-25.84, -4.74) * mm, "end": v(-24.71, -6.07) * mm});
            skLineSegment(sketch, "E341", {"start": v(-24.71, -6.07) * mm, "end": v(-22.87, -7.31) * mm});
            skLineSegment(sketch, "E342", {"start": v(-22.87, -7.31) * mm, "end": v(-20.62, -7.96) * mm});
            skLineSegment(sketch, "E343", {"start": v(-20.62, -7.96) * mm, "end": v(-18.65, -8.05) * mm});
            skLineSegment(sketch, "E344", {"start": v(-18.65, -8.05) * mm, "end": v(-18, -7.99) * mm});
            skLineSegment(sketch, "E345", {"start": v(-18, -7.99) * mm, "end": v(-17.32, -7.91) * mm});
            skLineSegment(sketch, "E346", {"start": v(-17.32, -7.91) * mm, "end": v(-15.3, -7.49) * mm});
            skLineSegment(sketch, "E347", {"start": v(-15.3, -7.49) * mm, "end": v(-12.8, -6.63) * mm});
            skLineSegment(sketch, "E348", {"start": v(-12.8, -6.63) * mm, "end": v(-10.47, -5.45) * mm});
            skLineSegment(sketch, "E349", {"start": v(-10.47, -5.45) * mm, "end": v(-8.3, -4.04) * mm});
            skLineSegment(sketch, "E350", {"start": v(-8.3, -4.04) * mm, "end": v(-6.26, -2.43) * mm});
            skLineSegment(sketch, "E351", {"start": v(-6.26, -2.43) * mm, "end": v(-4.34, -0.7) * mm});
            skLineSegment(sketch, "E352", {"start": v(-4.34, -0.7) * mm, "end": v(-2.51, 1.09) * mm});
            skLineSegment(sketch, "E353", {"start": v(-2.51, 1.09) * mm, "end": v(-1.2, 2.43) * mm});
            skLineSegment(sketch, "E354", {"start": v(-1.2, 2.43) * mm, "end": v(-0.77, 2.88) * mm});
            skLineSegment(sketch, "E355", {"start": v(-0.77, 2.88) * mm, "end": v(-0.5, 3.15) * mm});
            skLineSegment(sketch, "E356", {"start": v(-0.5, 3.15) * mm, "end": v(0.27, 3.97) * mm});
            skLineSegment(sketch, "E357", {"start": v(0.27, 3.97) * mm, "end": v(1.13, 4.87) * mm});
            skLineSegment(sketch, "E358", {"start": v(1.13, 4.87) * mm, "end": v(1.96, 5.7) * mm});
            skLineSegment(sketch, "E359", {"start": v(1.96, 5.7) * mm, "end": v(2.7, 6.36) * mm});
            skLineSegment(sketch, "E360", {"start": v(2.7, 6.36) * mm, "end": v(2.96, 6.57) * mm});
            skLineSegment(sketch, "E361", {"start": v(34.28, 6.37) * mm, "end": v(34.2, 6.34) * mm});
            skLineSegment(sketch, "E362", {"start": v(34.2, 6.34) * mm, "end": v(33.33, 6.02) * mm});
            skLineSegment(sketch, "E363", {"start": v(33.33, 6.02) * mm, "end": v(33.24, 6) * mm});
            skLineSegment(sketch, "E364", {"start": v(33.24, 6) * mm, "end": v(33.5, 5.68) * mm});
            skLineSegment(sketch, "E365", {"start": v(33.5, 5.68) * mm, "end": v(34.65, 3.98) * mm});
            skLineSegment(sketch, "E366", {"start": v(34.65, 3.98) * mm, "end": v(35.7, 2.15) * mm});
            skLineSegment(sketch, "E367", {"start": v(35.7, 2.15) * mm, "end": v(35.9, 1.76) * mm});
            skLineSegment(sketch, "E368", {"start": v(35.9, 1.76) * mm, "end": v(36.4, 0.73) * mm});
            skLineSegment(sketch, "E369", {"start": v(36.4, 0.73) * mm, "end": v(37.48, -2.6) * mm});
            skLineSegment(sketch, "E370", {"start": v(37.48, -2.6) * mm, "end": v(37.97, -6.91) * mm});
            skLineSegment(sketch, "E371", {"start": v(37.97, -6.91) * mm, "end": v(37.36, -11.1) * mm});
            skLineSegment(sketch, "E372", {"start": v(37.36, -11.1) * mm, "end": v(36.2, -14.15) * mm});
            skLineSegment(sketch, "E373", {"start": v(36.2, -14.15) * mm, "end": v(35.65, -15.07) * mm});
            skLineSegment(sketch, "E374", {"start": v(35.65, -15.07) * mm, "end": v(35.28, -15.69) * mm});
            skLineSegment(sketch, "E375", {"start": v(35.28, -15.69) * mm, "end": v(33.97, -17.43) * mm});
            skLineSegment(sketch, "E376", {"start": v(33.97, -17.43) * mm, "end": v(31.9, -19.56) * mm});
            skLineSegment(sketch, "E377", {"start": v(31.9, -19.56) * mm, "end": v(29.45, -21.42) * mm});
            skLineSegment(sketch, "E378", {"start": v(29.45, -21.42) * mm, "end": v(26.69, -23.01) * mm});
            skLineSegment(sketch, "E379", {"start": v(26.69, -23.01) * mm, "end": v(23.62, -24.31) * mm});
            skLineSegment(sketch, "E380", {"start": v(23.62, -24.31) * mm, "end": v(20.3, -25.3) * mm});
            skLineSegment(sketch, "E381", {"start": v(20.3, -25.3) * mm, "end": v(16.74, -25.97) * mm});
            skLineSegment(sketch, "E382", {"start": v(16.74, -25.97) * mm, "end": v(13.92, -26.26) * mm});
            skLineSegment(sketch, "E383", {"start": v(13.92, -26.26) * mm, "end": v(12.98, -26.3) * mm});
            skLineSegment(sketch, "E384", {"start": v(12.98, -26.3) * mm, "end": v(12.5, -26.32) * mm});
            skLineSegment(sketch, "E385", {"start": v(12.5, -26.32) * mm, "end": v(7.84, -26.33) * mm});
            skLineSegment(sketch, "E386", {"start": v(7.84, -26.33) * mm, "end": v(7.38, -26.3) * mm});
            skLineSegment(sketch, "E387", {"start": v(7.38, -26.3) * mm, "end": v(6.92, -26.3) * mm});
            skLineSegment(sketch, "E388", {"start": v(6.92, -26.3) * mm, "end": v(2.4, -25.95) * mm});
            skLineSegment(sketch, "E389", {"start": v(2.4, -25.95) * mm, "end": v(1.97, -25.9) * mm});
            skLineSegment(sketch, "E390", {"start": v(1.97, -25.9) * mm, "end": v(1.82, -25.97) * mm});
            skLineSegment(sketch, "E391", {"start": v(1.82, -25.97) * mm, "end": v(0.24, -26.66) * mm});
            skLineSegment(sketch, "E392", {"start": v(0.24, -26.66) * mm, "end": v(0.07, -26.72) * mm});
            skLineSegment(sketch, "E393", {"start": v(0.07, -26.72) * mm, "end": v(0.65, -26.8) * mm});
            skLineSegment(sketch, "E394", {"start": v(0.65, -26.8) * mm, "end": v(6.72, -27.35) * mm});
            skLineSegment(sketch, "E395", {"start": v(6.72, -27.35) * mm, "end": v(7.34, -27.37) * mm});
            skLineSegment(sketch, "E396", {"start": v(7.34, -27.37) * mm, "end": v(7.8, -27.4) * mm});
            skLineSegment(sketch, "E397", {"start": v(7.8, -27.4) * mm, "end": v(12.54, -27.38) * mm});
            skLineSegment(sketch, "E398", {"start": v(12.54, -27.38) * mm, "end": v(13.02, -27.36) * mm});
            skLineSegment(sketch, "E399", {"start": v(13.02, -27.36) * mm, "end": v(14, -27.32) * mm});
            skLineSegment(sketch, "E400", {"start": v(14, -27.32) * mm, "end": v(16.91, -27.02) * mm});
            skLineSegment(sketch, "E401", {"start": v(16.91, -27.02) * mm, "end": v(20.6, -26.32) * mm});
            skLineSegment(sketch, "E402", {"start": v(20.6, -26.32) * mm, "end": v(24.05, -25.29) * mm});
            skLineSegment(sketch, "E403", {"start": v(24.05, -25.29) * mm, "end": v(27.23, -23.93) * mm});
            skLineSegment(sketch, "E404", {"start": v(27.23, -23.93) * mm, "end": v(30.1, -22.26) * mm});
            skLineSegment(sketch, "E405", {"start": v(30.1, -22.26) * mm, "end": v(32.64, -20.31) * mm});
            skLineSegment(sketch, "E406", {"start": v(32.64, -20.31) * mm, "end": v(34.8, -18.09) * mm});
            skLineSegment(sketch, "E407", {"start": v(34.8, -18.09) * mm, "end": v(36.18, -16.26) * mm});
            skLineSegment(sketch, "E408", {"start": v(36.18, -16.26) * mm, "end": v(36.57, -15.6) * mm});
            skLineSegment(sketch, "E409", {"start": v(36.57, -15.6) * mm, "end": v(37.15, -14.63) * mm});
            skLineSegment(sketch, "E410", {"start": v(37.15, -14.63) * mm, "end": v(38.39, -11.4) * mm});
            skLineSegment(sketch, "E411", {"start": v(38.39, -11.4) * mm, "end": v(39.04, -6.96) * mm});
            skLineSegment(sketch, "E412", {"start": v(39.04, -6.96) * mm, "end": v(38.53, -2.37) * mm});
            skLineSegment(sketch, "E413", {"start": v(38.53, -2.37) * mm, "end": v(37.38, 1.14) * mm});
            skLineSegment(sketch, "E414", {"start": v(37.38, 1.14) * mm, "end": v(36.84, 2.23) * mm});
            skLineSegment(sketch, "E415", {"start": v(36.84, 2.23) * mm, "end": v(36.66, 2.6) * mm});
            skLineSegment(sketch, "E416", {"start": v(36.66, 2.6) * mm, "end": v(35.64, 4.4) * mm});
            skLineSegment(sketch, "E417", {"start": v(35.64, 4.4) * mm, "end": v(34.52, 6.05) * mm});
            skLineSegment(sketch, "E418", {"start": v(34.52, 6.05) * mm, "end": v(34.28, 6.37) * mm});
            skLineSegment(sketch, "E419", {"start": v(26.03, -9.82) * mm, "end": v(25.64, -10.14) * mm});
            skLineSegment(sketch, "E420", {"start": v(25.64, -10.14) * mm, "end": v(24.19, -10.8) * mm});
            skLineSegment(sketch, "E421", {"start": v(24.19, -10.8) * mm, "end": v(22.2, -11.22) * mm});
            skLineSegment(sketch, "E422", {"start": v(22.2, -11.22) * mm, "end": v(20.6, -11.3) * mm});
            skLineSegment(sketch, "E423", {"start": v(20.6, -11.3) * mm, "end": v(19.95, -11.3) * mm});
            skLineSegment(sketch, "E424", {"start": v(19.95, -11.3) * mm, "end": v(19.59, -11.28) * mm});
            skLineSegment(sketch, "E425", {"start": v(19.59, -11.28) * mm, "end": v(18.5, -11.18) * mm});
            skLineSegment(sketch, "E426", {"start": v(18.5, -11.18) * mm, "end": v(16.94, -10.82) * mm});
            skLineSegment(sketch, "E427", {"start": v(16.94, -10.82) * mm, "end": v(15.63, -10.09) * mm});
            skLineSegment(sketch, "E428", {"start": v(15.63, -10.09) * mm, "end": v(14.98, -9.18) * mm});
            skLineSegment(sketch, "E429", {"start": v(14.98, -9.18) * mm, "end": v(14.91, -8.85) * mm});
            skLineSegment(sketch, "E430", {"start": v(14.91, -8.85) * mm, "end": v(14.87, -8.64) * mm});
            skLineSegment(sketch, "E431", {"start": v(14.87, -8.64) * mm, "end": v(14.9, -8) * mm});
            skLineSegment(sketch, "E432", {"start": v(14.9, -8) * mm, "end": v(15.15, -7.35) * mm});
            skLineSegment(sketch, "E433", {"start": v(15.15, -7.35) * mm, "end": v(15.5, -6.89) * mm});
            skLineSegment(sketch, "E434", {"start": v(15.5, -6.89) * mm, "end": v(15.76, -6.67) * mm});
            skLineSegment(sketch, "E435", {"start": v(15.76, -6.67) * mm, "end": v(15.85, -6.6) * mm});
            skLineSegment(sketch, "E436", {"start": v(15.85, -6.6) * mm, "end": v(15.85, -6.6) * mm});
            skLineSegment(sketch, "E437", {"start": v(15.85, -6.6) * mm, "end": v(16.02, -6.5) * mm});
            skLineSegment(sketch, "E438", {"start": v(16.02, -6.5) * mm, "end": v(16.03, -6.5) * mm});
            skLineSegment(sketch, "E439", {"start": v(16.03, -6.5) * mm, "end": v(16.29, -6.42) * mm});
            skLineSegment(sketch, "E440", {"start": v(16.29, -6.42) * mm, "end": v(16.31, -6.42) * mm});
            skLineSegment(sketch, "E441", {"start": v(16.31, -6.42) * mm, "end": v(16.4, -6.42) * mm});
            skLineSegment(sketch, "E442", {"start": v(16.4, -6.42) * mm, "end": v(16.59, -6.56) * mm});
            skLineSegment(sketch, "E443", {"start": v(16.59, -6.56) * mm, "end": v(16.6, -6.7) * mm});
            skLineSegment(sketch, "E444", {"start": v(16.6, -6.7) * mm, "end": v(16.6, -6.74) * mm});
            skLineSegment(sketch, "E445", {"start": v(16.6, -6.74) * mm, "end": v(16.38, -7.02) * mm});
            skLineSegment(sketch, "E446", {"start": v(16.38, -7.02) * mm, "end": v(16.35, -7.05) * mm});
            skLineSegment(sketch, "E447", {"start": v(16.35, -7.05) * mm, "end": v(16.25, -7.12) * mm});
            skLineSegment(sketch, "E448", {"start": v(16.25, -7.12) * mm, "end": v(16.04, -7.5) * mm});
            skLineSegment(sketch, "E449", {"start": v(16.04, -7.5) * mm, "end": v(16.07, -7.75) * mm});
            skLineSegment(sketch, "E450", {"start": v(16.07, -7.75) * mm, "end": v(16.08, -7.77) * mm});
            skLineSegment(sketch, "E451", {"start": v(16.08, -7.77) * mm, "end": v(16.1, -7.83) * mm});
            skLineSegment(sketch, "E452", {"start": v(16.1, -7.83) * mm, "end": v(16.44, -8.11) * mm});
            skLineSegment(sketch, "E453", {"start": v(16.44, -8.11) * mm, "end": v(17.02, -8.3) * mm});
            skLineSegment(sketch, "E454", {"start": v(17.02, -8.3) * mm, "end": v(17.18, -8.3) * mm});
            skLineSegment(sketch, "E455", {"start": v(17.18, -8.3) * mm, "end": v(17.27, -8.3) * mm});
            skLineSegment(sketch, "E456", {"start": v(17.27, -8.3) * mm, "end": v(17.56, -8.27) * mm});
            skLineSegment(sketch, "E457", {"start": v(17.56, -8.27) * mm, "end": v(18.04, -8.15) * mm});
            skLineSegment(sketch, "E458", {"start": v(18.04, -8.15) * mm, "end": v(18.62, -7.92) * mm});
            skLineSegment(sketch, "E459", {"start": v(18.62, -7.92) * mm, "end": v(19.13, -7.63) * mm});
            skLineSegment(sketch, "E460", {"start": v(19.13, -7.63) * mm, "end": v(19.3, -7.52) * mm});
            skLineSegment(sketch, "E461", {"start": v(19.3, -7.52) * mm, "end": v(19.42, -7.43) * mm});
            skLineSegment(sketch, "E462", {"start": v(19.42, -7.43) * mm, "end": v(19.7, -7.23) * mm});
            skLineSegment(sketch, "E463", {"start": v(19.7, -7.23) * mm, "end": v(20.54, -6.67) * mm});
            skLineSegment(sketch, "E464", {"start": v(20.54, -6.67) * mm, "end": v(21.58, -6.1) * mm});
            skLineSegment(sketch, "E465", {"start": v(21.58, -6.1) * mm, "end": v(22.65, -5.72) * mm});
            skLineSegment(sketch, "E466", {"start": v(22.65, -5.72) * mm, "end": v(23.56, -5.59) * mm});
            skLineSegment(sketch, "E467", {"start": v(23.56, -5.59) * mm, "end": v(23.87, -5.59) * mm});
            skLineSegment(sketch, "E468", {"start": v(23.87, -5.59) * mm, "end": v(24.05, -5.59) * mm});
            skLineSegment(sketch, "E469", {"start": v(24.05, -5.59) * mm, "end": v(24.62, -5.64) * mm});
            skLineSegment(sketch, "E470", {"start": v(24.62, -5.64) * mm, "end": v(25.2, -5.76) * mm});
            skLineSegment(sketch, "E471", {"start": v(25.2, -5.76) * mm, "end": v(25.62, -5.94) * mm});
            skLineSegment(sketch, "E472", {"start": v(25.62, -5.94) * mm, "end": v(25.85, -6.08) * mm});
            skLineSegment(sketch, "E473", {"start": v(25.85, -6.08) * mm, "end": v(25.92, -6.14) * mm});
            skLineSegment(sketch, "E474", {"start": v(25.92, -6.14) * mm, "end": v(25.98, -6.07) * mm});
            skLineSegment(sketch, "E475", {"start": v(25.98, -6.07) * mm, "end": v(26.2, -5.87) * mm});
            skLineSegment(sketch, "E476", {"start": v(26.2, -5.87) * mm, "end": v(26.63, -5.63) * mm});
            skLineSegment(sketch, "E477", {"start": v(26.63, -5.63) * mm, "end": v(27.2, -5.44) * mm});
            skLineSegment(sketch, "E478", {"start": v(27.2, -5.44) * mm, "end": v(27.76, -5.35) * mm});
            skLineSegment(sketch, "E479", {"start": v(27.76, -5.35) * mm, "end": v(27.95, -5.35) * mm});
            skLineSegment(sketch, "E480", {"start": v(27.95, -5.35) * mm, "end": v(28.17, -5.34) * mm});
            skLineSegment(sketch, "E481", {"start": v(28.17, -5.34) * mm, "end": v(28.83, -5.4) * mm});
            skLineSegment(sketch, "E482", {"start": v(28.83, -5.4) * mm, "end": v(29.5, -5.6) * mm});
            skLineSegment(sketch, "E483", {"start": v(29.5, -5.6) * mm, "end": v(30, -5.89) * mm});
            skLineSegment(sketch, "E484", {"start": v(30, -5.89) * mm, "end": v(30.33, -6.14) * mm});
            skLineSegment(sketch, "E485", {"start": v(30.33, -6.14) * mm, "end": v(30.44, -6.23) * mm});
            skLineSegment(sketch, "E486", {"start": v(30.44, -6.23) * mm, "end": v(30.5, -6.28) * mm});
            skLineSegment(sketch, "E487", {"start": v(30.5, -6.28) * mm, "end": v(31.23, -6.78) * mm});
            skLineSegment(sketch, "E488", {"start": v(31.23, -6.78) * mm, "end": v(31.32, -6.82) * mm});
            skLineSegment(sketch, "E489", {"start": v(31.32, -6.82) * mm, "end": v(31.5, -6.9) * mm});
            skLineSegment(sketch, "E490", {"start": v(31.5, -6.9) * mm, "end": v(32.38, -7.22) * mm});
            skLineSegment(sketch, "E491", {"start": v(32.38, -7.22) * mm, "end": v(33.16, -7.36) * mm});
            skLineSegment(sketch, "E492", {"start": v(33.16, -7.36) * mm, "end": v(33.3, -7.36) * mm});
            skLineSegment(sketch, "E493", {"start": v(33.3, -7.36) * mm, "end": v(33.46, -7.37) * mm});
            skLineSegment(sketch, "E494", {"start": v(33.46, -7.37) * mm, "end": v(34.12, -7.22) * mm});
            skLineSegment(sketch, "E495", {"start": v(34.12, -7.22) * mm, "end": v(34.52, -6.88) * mm});
            skLineSegment(sketch, "E496", {"start": v(34.52, -6.88) * mm, "end": v(34.56, -6.78) * mm});
            skLineSegment(sketch, "E497", {"start": v(34.56, -6.78) * mm, "end": v(34.57, -6.77) * mm});
            skLineSegment(sketch, "E498", {"start": v(34.57, -6.77) * mm, "end": v(34.58, -6.69) * mm});
            skLineSegment(sketch, "E499", {"start": v(34.58, -6.69) * mm, "end": v(34.57, -6.52) * mm});
            skLineSegment(sketch, "E500", {"start": v(34.57, -6.52) * mm, "end": v(34.47, -6.31) * mm});
            skLineSegment(sketch, "E501", {"start": v(34.47, -6.31) * mm, "end": v(34.3, -6.13) * mm});
            skLineSegment(sketch, "E502", {"start": v(34.3, -6.13) * mm, "end": v(34.23, -6.09) * mm});
            skLineSegment(sketch, "E503", {"start": v(34.23, -6.09) * mm, "end": v(34.19, -6.07) * mm});
            skLineSegment(sketch, "E504", {"start": v(34.19, -6.07) * mm, "end": v(33.95, -5.8) * mm});
            skLineSegment(sketch, "E505", {"start": v(33.95, -5.8) * mm, "end": v(33.95, -5.77) * mm});
            skLineSegment(sketch, "E506", {"start": v(33.95, -5.77) * mm, "end": v(33.94, -5.65) * mm});
            skLineSegment(sketch, "E507", {"start": v(33.94, -5.65) * mm, "end": v(34.03, -5.54) * mm});
            skLineSegment(sketch, "E508", {"start": v(34.03, -5.54) * mm, "end": v(34.04, -5.54) * mm});
            skLineSegment(sketch, "E509", {"start": v(34.04, -5.54) * mm, "end": v(34.22, -5.46) * mm});
            skLineSegment(sketch, "E510", {"start": v(34.22, -5.46) * mm, "end": v(34.25, -5.46) * mm});
            skLineSegment(sketch, "E511", {"start": v(34.25, -5.46) * mm, "end": v(34.27, -5.46) * mm});
            skLineSegment(sketch, "E512", {"start": v(34.27, -5.46) * mm, "end": v(34.51, -5.53) * mm});
            skLineSegment(sketch, "E513", {"start": v(34.51, -5.53) * mm, "end": v(34.53, -5.53) * mm});
            skLineSegment(sketch, "E514", {"start": v(34.53, -5.53) * mm, "end": v(34.62, -5.58) * mm});
            skLineSegment(sketch, "E515", {"start": v(34.62, -5.58) * mm, "end": v(34.71, -5.63) * mm});
            skLineSegment(sketch, "E516", {"start": v(34.71, -5.63) * mm, "end": v(34.98, -5.8) * mm});
            skLineSegment(sketch, "E517", {"start": v(34.98, -5.8) * mm, "end": v(35.4, -6.23) * mm});
            skLineSegment(sketch, "E518", {"start": v(35.4, -6.23) * mm, "end": v(35.74, -6.87) * mm});
            skLineSegment(sketch, "E519", {"start": v(35.74, -6.87) * mm, "end": v(35.84, -7.54) * mm});
            skLineSegment(sketch, "E520", {"start": v(35.84, -7.54) * mm, "end": v(35.82, -7.75) * mm});
            skLineSegment(sketch, "E521", {"start": v(35.82, -7.75) * mm, "end": v(35.78, -8.1) * mm});
            skLineSegment(sketch, "E522", {"start": v(35.78, -8.1) * mm, "end": v(35.2, -9.07) * mm});
            skLineSegment(sketch, "E523", {"start": v(35.2, -9.07) * mm, "end": v(33.92, -9.92) * mm});
            skLineSegment(sketch, "E524", {"start": v(33.92, -9.92) * mm, "end": v(32.4, -10.42) * mm});
            skLineSegment(sketch, "E525", {"start": v(32.4, -10.42) * mm, "end": v(31.37, -10.6) * mm});
            skLineSegment(sketch, "E526", {"start": v(31.37, -10.6) * mm, "end": v(31.02, -10.65) * mm});
            skLineSegment(sketch, "E527", {"start": v(31.02, -10.65) * mm, "end": v(30.4, -10.67) * mm});
            skLineSegment(sketch, "E528", {"start": v(30.4, -10.67) * mm, "end": v(28.53, -10.57) * mm});
            skLineSegment(sketch, "E529", {"start": v(28.53, -10.57) * mm, "end": v(27, -10.28) * mm});
            skLineSegment(sketch, "E530", {"start": v(27, -10.28) * mm, "end": v(26.24, -9.96) * mm});
            skLineSegment(sketch, "E531", {"start": v(26.24, -9.96) * mm, "end": v(26.03, -9.82) * mm});
            skLineSegment(sketch, "E532", {"start": v(18.27, 2.08) * mm, "end": v(18.08, 2.08) * mm});
            skLineSegment(sketch, "E533", {"start": v(18.08, 2.08) * mm, "end": v(17.53, 2.03) * mm});
            skLineSegment(sketch, "E534", {"start": v(17.53, 2.03) * mm, "end": v(16.85, 1.84) * mm});
            skLineSegment(sketch, "E535", {"start": v(16.85, 1.84) * mm, "end": v(16.22, 1.53) * mm});
            skLineSegment(sketch, "E536", {"start": v(16.22, 1.53) * mm, "end": v(15.67, 1.1) * mm});
            skLineSegment(sketch, "E537", {"start": v(15.67, 1.1) * mm, "end": v(15.2, 0.59) * mm});
            skLineSegment(sketch, "E538", {"start": v(15.2, 0.59) * mm, "end": v(14.85, -0.02) * mm});
            skLineSegment(sketch, "E539", {"start": v(14.85, -0.02) * mm, "end": v(14.61, -0.69) * mm});
            skLineSegment(sketch, "E540", {"start": v(14.61, -0.69) * mm, "end": v(14.52, -1.23) * mm});
            skLineSegment(sketch, "E541", {"start": v(14.52, -1.23) * mm, "end": v(14.51, -1.41) * mm});
            skLineSegment(sketch, "E542", {"start": v(14.51, -1.41) * mm, "end": v(14.5, -1.6) * mm});
            skLineSegment(sketch, "E543", {"start": v(14.5, -1.6) * mm, "end": v(14.56, -2.15) * mm});
            skLineSegment(sketch, "E544", {"start": v(14.56, -2.15) * mm, "end": v(14.75, -2.83) * mm});
            skLineSegment(sketch, "E545", {"start": v(14.75, -2.83) * mm, "end": v(15.06, -3.46) * mm});
            skLineSegment(sketch, "E546", {"start": v(15.06, -3.46) * mm, "end": v(15.48, -4.01) * mm});
            skLineSegment(sketch, "E547", {"start": v(15.48, -4.01) * mm, "end": v(16, -4.48) * mm});
            skLineSegment(sketch, "E548", {"start": v(16, -4.48) * mm, "end": v(16.6, -4.83) * mm});
            skLineSegment(sketch, "E549", {"start": v(16.6, -4.83) * mm, "end": v(17.28, -5.07) * mm});
            skLineSegment(sketch, "E550", {"start": v(17.28, -5.07) * mm, "end": v(17.82, -5.16) * mm});
            skLineSegment(sketch, "E551", {"start": v(17.82, -5.16) * mm, "end": v(18, -5.17) * mm});
            skLineSegment(sketch, "E552", {"start": v(18, -5.17) * mm, "end": v(18.18, -5.17) * mm});
            skLineSegment(sketch, "E553", {"start": v(18.18, -5.17) * mm, "end": v(18.73, -5.12) * mm});
            skLineSegment(sketch, "E554", {"start": v(18.73, -5.12) * mm, "end": v(19.42, -4.93) * mm});
            skLineSegment(sketch, "E555", {"start": v(19.42, -4.93) * mm, "end": v(20.05, -4.62) * mm});
            skLineSegment(sketch, "E556", {"start": v(20.05, -4.62) * mm, "end": v(20.6, -4.2) * mm});
            skLineSegment(sketch, "E557", {"start": v(20.6, -4.2) * mm, "end": v(21.06, -3.68) * mm});
            skLineSegment(sketch, "E558", {"start": v(21.06, -3.68) * mm, "end": v(21.42, -3.08) * mm});
            skLineSegment(sketch, "E559", {"start": v(21.42, -3.08) * mm, "end": v(21.66, -2.4) * mm});
            skLineSegment(sketch, "E560", {"start": v(21.66, -2.4) * mm, "end": v(21.75, -1.86) * mm});
            skLineSegment(sketch, "E561", {"start": v(21.75, -1.86) * mm, "end": v(21.76, -1.68) * mm});
            skLineSegment(sketch, "E562", {"start": v(21.76, -1.68) * mm, "end": v(21.76, -1.5) * mm});
            skLineSegment(sketch, "E563", {"start": v(21.76, -1.5) * mm, "end": v(21.7, -0.95) * mm});
            skLineSegment(sketch, "E564", {"start": v(21.7, -0.95) * mm, "end": v(21.52, -0.26) * mm});
            skLineSegment(sketch, "E565", {"start": v(21.52, -0.26) * mm, "end": v(21.21, 0.37) * mm});
            skLineSegment(sketch, "E566", {"start": v(21.21, 0.37) * mm, "end": v(20.79, 0.92) * mm});
            skLineSegment(sketch, "E567", {"start": v(20.79, 0.92) * mm, "end": v(20.27, 1.38) * mm});
            skLineSegment(sketch, "E568", {"start": v(20.27, 1.38) * mm, "end": v(19.66, 1.74) * mm});
            skLineSegment(sketch, "E569", {"start": v(19.66, 1.74) * mm, "end": v(19, 1.98) * mm});
            skLineSegment(sketch, "E570", {"start": v(19, 1.98) * mm, "end": v(18.45, 2.07) * mm});
            skLineSegment(sketch, "E571", {"start": v(18.45, 2.07) * mm, "end": v(18.27, 2.08) * mm});
            skLineSegment(sketch, "E572", {"start": v(17.98, -5.7) * mm, "end": v(17.77, -5.7) * mm});
            skLineSegment(sketch, "E573", {"start": v(17.77, -5.7) * mm, "end": v(17.15, -5.58) * mm});
            skLineSegment(sketch, "E574", {"start": v(17.15, -5.58) * mm, "end": v(16.38, -5.31) * mm});
            skLineSegment(sketch, "E575", {"start": v(16.38, -5.31) * mm, "end": v(15.69, -4.9) * mm});
            skLineSegment(sketch, "E576", {"start": v(15.69, -4.9) * mm, "end": v(15.1, -4.37) * mm});
            skLineSegment(sketch, "E577", {"start": v(15.1, -4.37) * mm, "end": v(14.6, -3.74) * mm});
            skLineSegment(sketch, "E578", {"start": v(14.6, -3.74) * mm, "end": v(14.25, -3.02) * mm});
            skLineSegment(sketch, "E579", {"start": v(14.25, -3.02) * mm, "end": v(14.03, -2.23) * mm});
            skLineSegment(sketch, "E580", {"start": v(14.03, -2.23) * mm, "end": v(13.97, -1.6) * mm});
            skLineSegment(sketch, "E581", {"start": v(13.97, -1.6) * mm, "end": v(13.98, -1.4) * mm});
            skLineSegment(sketch, "E582", {"start": v(13.98, -1.4) * mm, "end": v(13.99, -1.19) * mm});
            skLineSegment(sketch, "E583", {"start": v(13.99, -1.19) * mm, "end": v(14.1, -0.56) * mm});
            skLineSegment(sketch, "E584", {"start": v(14.1, -0.56) * mm, "end": v(14.36, 0.2) * mm});
            skLineSegment(sketch, "E585", {"start": v(14.36, 0.2) * mm, "end": v(14.77, 0.9) * mm});
            skLineSegment(sketch, "E586", {"start": v(14.77, 0.9) * mm, "end": v(15.3, 1.5) * mm});
            skLineSegment(sketch, "E587", {"start": v(15.3, 1.5) * mm, "end": v(15.94, 1.98) * mm});
            skLineSegment(sketch, "E588", {"start": v(15.94, 1.98) * mm, "end": v(16.66, 2.34) * mm});
            skLineSegment(sketch, "E589", {"start": v(16.66, 2.34) * mm, "end": v(17.45, 2.55) * mm});
            skLineSegment(sketch, "E590", {"start": v(17.45, 2.55) * mm, "end": v(18.08, 2.62) * mm});
            skLineSegment(sketch, "E591", {"start": v(18.08, 2.62) * mm, "end": v(18.29, 2.6) * mm});
            skLineSegment(sketch, "E592", {"start": v(18.29, 2.6) * mm, "end": v(18.5, 2.6) * mm});
            skLineSegment(sketch, "E593", {"start": v(18.5, 2.6) * mm, "end": v(19.12, 2.5) * mm});
            skLineSegment(sketch, "E594", {"start": v(19.12, 2.5) * mm, "end": v(19.89, 2.22) * mm});
            skLineSegment(sketch, "E595", {"start": v(19.89, 2.22) * mm, "end": v(20.58, 1.81) * mm});
            skLineSegment(sketch, "E596", {"start": v(20.58, 1.81) * mm, "end": v(21.18, 1.28) * mm});
            skLineSegment(sketch, "E597", {"start": v(21.18, 1.28) * mm, "end": v(21.66, 0.65) * mm});
            skLineSegment(sketch, "E598", {"start": v(21.66, 0.65) * mm, "end": v(22.02, -0.07) * mm});
            skLineSegment(sketch, "E599", {"start": v(22.02, -0.07) * mm, "end": v(22.23, -0.86) * mm});
            skLineSegment(sketch, "E600", {"start": v(22.23, -0.86) * mm, "end": v(22.3, -1.49) * mm});
            skLineSegment(sketch, "E601", {"start": v(22.3, -1.49) * mm, "end": v(22.29, -1.7) * mm});
            skLineSegment(sketch, "E602", {"start": v(22.29, -1.7) * mm, "end": v(22.28, -1.9) * mm});
            skLineSegment(sketch, "E603", {"start": v(22.28, -1.9) * mm, "end": v(22.17, -2.53) * mm});
            skLineSegment(sketch, "E604", {"start": v(22.17, -2.53) * mm, "end": v(21.9, -3.3) * mm});
            skLineSegment(sketch, "E605", {"start": v(21.9, -3.3) * mm, "end": v(21.5, -4) * mm});
            skLineSegment(sketch, "E606", {"start": v(21.5, -4) * mm, "end": v(20.96, -4.59) * mm});
            skLineSegment(sketch, "E607", {"start": v(20.96, -4.59) * mm, "end": v(20.33, -5.07) * mm});
            skLineSegment(sketch, "E608", {"start": v(20.33, -5.07) * mm, "end": v(19.61, -5.43) * mm});
            skLineSegment(sketch, "E609", {"start": v(19.61, -5.43) * mm, "end": v(18.82, -5.65) * mm});
            skLineSegment(sketch, "E610", {"start": v(18.82, -5.65) * mm, "end": v(18.2, -5.7) * mm});
            skLineSegment(sketch, "E611", {"start": v(18.2, -5.7) * mm, "end": v(17.98, -5.7) * mm});
            skLineSegment(sketch, "E612", {"start": v(11, -8.73) * mm, "end": v(10.96, -8.73) * mm});
            skLineSegment(sketch, "E613", {"start": v(10.96, -8.73) * mm, "end": v(10.8, -8.65) * mm});
            skLineSegment(sketch, "E614", {"start": v(10.8, -8.65) * mm, "end": v(10.74, -8.5) * mm});
            skLineSegment(sketch, "E615", {"start": v(10.74, -8.5) * mm, "end": v(10.74, -8.46) * mm});
            skLineSegment(sketch, "E616", {"start": v(10.74, -8.46) * mm, "end": v(10.74, -8.42) * mm});
            skLineSegment(sketch, "E617", {"start": v(10.74, -8.42) * mm, "end": v(10.75, -8.25) * mm});
            skLineSegment(sketch, "E618", {"start": v(10.75, -8.25) * mm, "end": v(10.82, -7.8) * mm});
            skLineSegment(sketch, "E619", {"start": v(10.82, -7.8) * mm, "end": v(10.98, -7.14) * mm});
            skLineSegment(sketch, "E620", {"start": v(10.98, -7.14) * mm, "end": v(11.27, -6.35) * mm});
            skLineSegment(sketch, "E621", {"start": v(11.27, -6.35) * mm, "end": v(11.73, -5.49) * mm});
            skLineSegment(sketch, "E622", {"start": v(11.73, -5.49) * mm, "end": v(12.4, -4.61) * mm});
            skLineSegment(sketch, "E623", {"start": v(12.4, -4.61) * mm, "end": v(13.3, -3.8) * mm});
            skLineSegment(sketch, "E624", {"start": v(13.3, -3.8) * mm, "end": v(14.17, -3.23) * mm});
            skLineSegment(sketch, "E625", {"start": v(14.17, -3.23) * mm, "end": v(14.49, -3.08) * mm});
            skLineSegment(sketch, "E626", {"start": v(14.49, -3.08) * mm, "end": v(14.52, -3.06) * mm});
            skLineSegment(sketch, "E627", {"start": v(14.52, -3.06) * mm, "end": v(14.69, -3.07) * mm});
            skLineSegment(sketch, "E628", {"start": v(14.69, -3.07) * mm, "end": v(14.83, -3.17) * mm});
            skLineSegment(sketch, "E629", {"start": v(14.83, -3.17) * mm, "end": v(14.84, -3.2) * mm});
            skLineSegment(sketch, "E630", {"start": v(14.84, -3.2) * mm, "end": v(14.86, -3.24) * mm});
            skLineSegment(sketch, "E631", {"start": v(14.86, -3.24) * mm, "end": v(14.85, -3.4) * mm});
            skLineSegment(sketch, "E632", {"start": v(14.85, -3.4) * mm, "end": v(14.75, -3.55) * mm});
            skLineSegment(sketch, "E633", {"start": v(14.75, -3.55) * mm, "end": v(14.71, -3.56) * mm});
            skLineSegment(sketch, "E634", {"start": v(14.71, -3.56) * mm, "end": v(14.43, -3.7) * mm});
            skLineSegment(sketch, "E635", {"start": v(14.43, -3.7) * mm, "end": v(13.63, -4.21) * mm});
            skLineSegment(sketch, "E636", {"start": v(13.63, -4.21) * mm, "end": v(12.8, -4.97) * mm});
            skLineSegment(sketch, "E637", {"start": v(12.8, -4.97) * mm, "end": v(12.19, -5.76) * mm});
            skLineSegment(sketch, "E638", {"start": v(12.19, -5.76) * mm, "end": v(11.77, -6.55) * mm});
            skLineSegment(sketch, "E639", {"start": v(11.77, -6.55) * mm, "end": v(11.5, -7.27) * mm});
            skLineSegment(sketch, "E640", {"start": v(11.5, -7.27) * mm, "end": v(11.35, -7.87) * mm});
            skLineSegment(sketch, "E641", {"start": v(11.35, -7.87) * mm, "end": v(11.28, -8.3) * mm});
            skLineSegment(sketch, "E642", {"start": v(11.28, -8.3) * mm, "end": v(11.27, -8.44) * mm});
            skLineSegment(sketch, "E643", {"start": v(11.27, -8.44) * mm, "end": v(11.27, -8.48) * mm});
            skLineSegment(sketch, "E644", {"start": v(11.27, -8.48) * mm, "end": v(11.27, -8.52) * mm});
            skLineSegment(sketch, "E645", {"start": v(11.27, -8.52) * mm, "end": v(11.18, -8.66) * mm});
            skLineSegment(sketch, "E646", {"start": v(11.18, -8.66) * mm, "end": v(11.03, -8.74) * mm});
            skLineSegment(sketch, "E647", {"start": v(11.03, -8.74) * mm, "end": v(11, -8.73) * mm});
            skLineSegment(sketch, "E648", {"start": v(18.1, -3.58) * mm, "end": v(17.94, -3.57) * mm});
            skLineSegment(sketch, "E649", {"start": v(17.94, -3.57) * mm, "end": v(17.47, -3.4) * mm});
            skLineSegment(sketch, "E650", {"start": v(17.47, -3.4) * mm, "end": v(16.95, -2.98) * mm});
            skLineSegment(sketch, "E651", {"start": v(16.95, -2.98) * mm, "end": v(16.6, -2.36) * mm});
            skLineSegment(sketch, "E652", {"start": v(16.6, -2.36) * mm, "end": v(16.45, -1.8) * mm});
            skLineSegment(sketch, "E653", {"start": v(16.45, -1.8) * mm, "end": v(16.44, -1.6) * mm});
            skLineSegment(sketch, "E654", {"start": v(16.44, -1.6) * mm, "end": v(16.44, -1.47) * mm});
            skLineSegment(sketch, "E655", {"start": v(16.44, -1.47) * mm, "end": v(16.54, -0.83) * mm});
            skLineSegment(sketch, "E656", {"start": v(16.54, -0.83) * mm, "end": v(16.8, -0.27) * mm});
            skLineSegment(sketch, "E657", {"start": v(16.8, -0.27) * mm, "end": v(16.87, -0.17) * mm});
            skLineSegment(sketch, "E658", {"start": v(16.87, -0.17) * mm, "end": v(16.95, -0.07) * mm});
            skLineSegment(sketch, "E659", {"start": v(16.95, -0.07) * mm, "end": v(17.41, 0.3) * mm});
            skLineSegment(sketch, "E660", {"start": v(17.41, 0.3) * mm, "end": v(17.95, 0.48) * mm});
            skLineSegment(sketch, "E661", {"start": v(17.95, 0.48) * mm, "end": v(18.07, 0.49) * mm});
            skLineSegment(sketch, "E662", {"start": v(18.07, 0.49) * mm, "end": v(18.23, 0.5) * mm});
            skLineSegment(sketch, "E663", {"start": v(18.23, 0.5) * mm, "end": v(18.73, 0.35) * mm});
            skLineSegment(sketch, "E664", {"start": v(18.73, 0.35) * mm, "end": v(19.28, -0.07) * mm});
            skLineSegment(sketch, "E665", {"start": v(19.28, -0.07) * mm, "end": v(19.67, -0.7) * mm});
            skLineSegment(sketch, "E666", {"start": v(19.67, -0.7) * mm, "end": v(19.82, -1.3) * mm});
            skLineSegment(sketch, "E667", {"start": v(19.82, -1.3) * mm, "end": v(19.83, -1.5) * mm});
            skLineSegment(sketch, "E668", {"start": v(19.83, -1.5) * mm, "end": v(19.83, -1.62) * mm});
            skLineSegment(sketch, "E669", {"start": v(19.83, -1.62) * mm, "end": v(19.73, -2.26) * mm});
            skLineSegment(sketch, "E670", {"start": v(19.73, -2.26) * mm, "end": v(19.47, -2.82) * mm});
            skLineSegment(sketch, "E671", {"start": v(19.47, -2.82) * mm, "end": v(19.4, -2.92) * mm});
            skLineSegment(sketch, "E672", {"start": v(19.4, -2.92) * mm, "end": v(19.32, -3.02) * mm});
            skLineSegment(sketch, "E673", {"start": v(19.32, -3.02) * mm, "end": v(18.86, -3.4) * mm});
            skLineSegment(sketch, "E674", {"start": v(18.86, -3.4) * mm, "end": v(18.32, -3.58) * mm});
            skLineSegment(sketch, "E675", {"start": v(18.32, -3.58) * mm, "end": v(18.2, -3.58) * mm});
            skLineSegment(sketch, "E676", {"start": v(18.2, -3.58) * mm, "end": v(18.2, -3.58) * mm});
            skLineSegment(sketch, "E677", {"start": v(18.2, -3.58) * mm, "end": v(18.1, -3.58) * mm});
            skLineSegment(sketch, "E678", {"start": v(18.1, -3.58) * mm, "end": v(18.1, -3.58) * mm});
            skLineSegment(sketch, "E679", {"start": v(32.6, -2.4) * mm, "end": v(32.45, -2.4) * mm});
            skLineSegment(sketch, "E680", {"start": v(32.45, -2.4) * mm, "end": v(32, -2.24) * mm});
            skLineSegment(sketch, "E681", {"start": v(32, -2.24) * mm, "end": v(31.53, -1.84) * mm});
            skLineSegment(sketch, "E682", {"start": v(31.53, -1.84) * mm, "end": v(31.2, -1.25) * mm});
            skLineSegment(sketch, "E683", {"start": v(31.2, -1.25) * mm, "end": v(31.1, -0.71) * mm});
            skLineSegment(sketch, "E684", {"start": v(31.1, -0.71) * mm, "end": v(31.1, -0.53) * mm});
            skLineSegment(sketch, "E685", {"start": v(31.1, -0.53) * mm, "end": v(31.1, -0.36) * mm});
            skLineSegment(sketch, "E686", {"start": v(31.1, -0.36) * mm, "end": v(31.2, 0.17) * mm});
            skLineSegment(sketch, "E687", {"start": v(31.2, 0.17) * mm, "end": v(31.46, 0.68) * mm});
            skLineSegment(sketch, "E688", {"start": v(31.46, 0.68) * mm, "end": v(31.53, 0.77) * mm});
            skLineSegment(sketch, "E689", {"start": v(31.53, 0.77) * mm, "end": v(31.6, 0.86) * mm});
            skLineSegment(sketch, "E690", {"start": v(31.6, 0.86) * mm, "end": v(32.04, 1.19) * mm});
            skLineSegment(sketch, "E691", {"start": v(32.04, 1.19) * mm, "end": v(32.5, 1.34) * mm});
            skLineSegment(sketch, "E692", {"start": v(32.5, 1.34) * mm, "end": v(32.65, 1.34) * mm});
            skLineSegment(sketch, "E693", {"start": v(32.65, 1.34) * mm, "end": v(32.7, 1.33) * mm});
            skLineSegment(sketch, "E694", {"start": v(32.7, 1.33) * mm, "end": v(32.85, 1.33) * mm});
            skLineSegment(sketch, "E695", {"start": v(32.85, 1.33) * mm, "end": v(33.3, 1.17) * mm});
            skLineSegment(sketch, "E696", {"start": v(33.3, 1.17) * mm, "end": v(33.77, 0.77) * mm});
            skLineSegment(sketch, "E697", {"start": v(33.77, 0.77) * mm, "end": v(34.1, 0.18) * mm});
            skLineSegment(sketch, "E698", {"start": v(34.1, 0.18) * mm, "end": v(34.2, -0.36) * mm});
            skLineSegment(sketch, "E699", {"start": v(34.2, -0.36) * mm, "end": v(34.2, -0.54) * mm});
            skLineSegment(sketch, "E700", {"start": v(34.2, -0.54) * mm, "end": v(34.2, -0.66) * mm});
            skLineSegment(sketch, "E701", {"start": v(34.2, -0.66) * mm, "end": v(34.1, -1.24) * mm});
            skLineSegment(sketch, "E702", {"start": v(34.1, -1.24) * mm, "end": v(33.84, -1.75) * mm});
            skLineSegment(sketch, "E703", {"start": v(33.84, -1.75) * mm, "end": v(33.77, -1.84) * mm});
            skLineSegment(sketch, "E704", {"start": v(33.77, -1.84) * mm, "end": v(33.7, -1.93) * mm});
            skLineSegment(sketch, "E705", {"start": v(33.7, -1.93) * mm, "end": v(33.26, -2.26) * mm});
            skLineSegment(sketch, "E706", {"start": v(33.26, -2.26) * mm, "end": v(32.75, -2.4) * mm});
            skLineSegment(sketch, "E707", {"start": v(32.75, -2.4) * mm, "end": v(32.65, -2.4) * mm});
            skLineSegment(sketch, "E708", {"start": v(32.65, -2.4) * mm, "end": v(32.6, -2.4) * mm});
            skLineSegment(sketch, "E709", {"start": v(34.33, 9.93) * mm, "end": v(34.3, 10.1) * mm});
            skLineSegment(sketch, "E710", {"start": v(34.3, 10.1) * mm, "end": v(33.98, 10.55) * mm});
            skLineSegment(sketch, "E711", {"start": v(33.98, 10.55) * mm, "end": v(33.3, 10.98) * mm});
            skLineSegment(sketch, "E712", {"start": v(33.3, 10.98) * mm, "end": v(32.43, 11.27) * mm});
            skLineSegment(sketch, "E713", {"start": v(32.43, 11.27) * mm, "end": v(31.77, 11.41) * mm});
            skLineSegment(sketch, "E714", {"start": v(31.67, 11.43) * mm, "end": v(31.43, 11.28) * mm});
            skLineSegment(sketch, "E715", {"start": v(31.43, 11.28) * mm, "end": v(30.71, 10.84) * mm});
            skLineSegment(sketch, "E716", {"start": v(30.71, 10.84) * mm, "end": v(29.46, 10.2) * mm});
            skLineSegment(sketch, "E717", {"start": v(29.46, 10.2) * mm, "end": v(27.83, 9.62) * mm});
            skLineSegment(sketch, "E718", {"start": v(27.83, 9.62) * mm, "end": v(26.25, 9.25) * mm});
            skLineSegment(sketch, "E719", {"start": v(26.25, 9.25) * mm, "end": v(25.72, 9.17) * mm});
            skLineSegment(sketch, "E720", {"start": v(25.72, 9.17) * mm, "end": v(24.85, 9.05) * mm});
            skLineSegment(sketch, "E721", {"start": v(24.85, 9.05) * mm, "end": v(22.24, 8.8) * mm});
            skLineSegment(sketch, "E722", {"start": v(22.24, 8.8) * mm, "end": v(18.9, 8.68) * mm});
            skLineSegment(sketch, "E723", {"start": v(18.9, 8.68) * mm, "end": v(15.73, 8.8) * mm});
            skLineSegment(sketch, "E724", {"start": v(15.73, 8.8) * mm, "end": v(12.83, 9.13) * mm});
            skLineSegment(sketch, "E725", {"start": v(12.83, 9.13) * mm, "end": v(10.23, 9.64) * mm});
            skLineSegment(sketch, "E726", {"start": v(10.23, 9.64) * mm, "end": v(8, 10.31) * mm});
            skLineSegment(sketch, "E727", {"start": v(8, 10.31) * mm, "end": v(6.2, 11.13) * mm});
            skLineSegment(sketch, "E728", {"start": v(6.2, 11.13) * mm, "end": v(5.17, 11.79) * mm});
            skLineSegment(sketch, "E729", {"start": v(5.17, 11.79) * mm, "end": v(4.87, 12.06) * mm});
            skLineSegment(sketch, "E730", {"start": v(4.87, 12.06) * mm, "end": v(4.68, 12.04) * mm});
            skLineSegment(sketch, "E731", {"start": v(4.68, 12.04) * mm, "end": v(4.1, 11.95) * mm});
            skLineSegment(sketch, "E732", {"start": v(4.1, 11.95) * mm, "end": v(3.2, 11.72) * mm});
            skLineSegment(sketch, "E733", {"start": v(3.2, 11.72) * mm, "end": v(2.42, 11.33) * mm});
            skLineSegment(sketch, "E734", {"start": v(2.42, 11.33) * mm, "end": v(2, 10.9) * mm});
            skLineSegment(sketch, "E735", {"start": v(2, 10.9) * mm, "end": v(1.95, 10.73) * mm});
            skLineSegment(sketch, "E736", {"start": v(1.95, 10.73) * mm, "end": v(1.92, 10.6) * mm});
            skLineSegment(sketch, "E737", {"start": v(1.92, 10.6) * mm, "end": v(2.03, 9.98) * mm});
            skLineSegment(sketch, "E738", {"start": v(2.03, 9.98) * mm, "end": v(2.54, 9.33) * mm});
            skLineSegment(sketch, "E739", {"start": v(2.54, 9.33) * mm, "end": v(2.7, 9.2) * mm});
            skLineSegment(sketch, "E740", {"start": v(2.7, 9.2) * mm, "end": v(2.93, 9.01) * mm});
            skLineSegment(sketch, "E741", {"start": v(2.93, 9.01) * mm, "end": v(3.68, 8.5) * mm});
            skLineSegment(sketch, "E742", {"start": v(3.68, 8.5) * mm, "end": v(4.89, 7.86) * mm});
            skLineSegment(sketch, "E743", {"start": v(4.89, 7.86) * mm, "end": v(6.39, 7.27) * mm});
            skLineSegment(sketch, "E744", {"start": v(6.39, 7.27) * mm, "end": v(8.24, 6.75) * mm});
            skLineSegment(sketch, "E745", {"start": v(8.24, 6.75) * mm, "end": v(10.5, 6.31) * mm});
            skLineSegment(sketch, "E746", {"start": v(10.5, 6.31) * mm, "end": v(13.2, 5.97) * mm});
            skLineSegment(sketch, "E747", {"start": v(13.2, 5.97) * mm, "end": v(16.44, 5.75) * mm});
            skLineSegment(sketch, "E748", {"start": v(16.44, 5.75) * mm, "end": v(19.29, 5.65) * mm});
            skLineSegment(sketch, "E749", {"start": v(19.29, 5.65) * mm, "end": v(20.24, 5.64) * mm});
            skLineSegment(sketch, "E750", {"start": v(20.24, 5.64) * mm, "end": v(20.24, 5.64) * mm});
            skLineSegment(sketch, "E751", {"start": v(20.24, 5.64) * mm, "end": v(20.62, 5.66) * mm});
            skLineSegment(sketch, "E752", {"start": v(20.62, 5.66) * mm, "end": v(21.77, 5.7) * mm});
            skLineSegment(sketch, "E753", {"start": v(21.77, 5.7) * mm, "end": v(23.52, 5.8) * mm});
            skLineSegment(sketch, "E754", {"start": v(23.52, 5.8) * mm, "end": v(25.4, 5.95) * mm});
            skLineSegment(sketch, "E755", {"start": v(25.4, 5.95) * mm, "end": v(27.32, 6.18) * mm});
            skLineSegment(sketch, "E756", {"start": v(27.32, 6.18) * mm, "end": v(29.2, 6.52) * mm});
            skLineSegment(sketch, "E757", {"start": v(29.2, 6.52) * mm, "end": v(30.93, 7) * mm});
            skLineSegment(sketch, "E758", {"start": v(30.93, 7) * mm, "end": v(32.45, 7.64) * mm});
            skLineSegment(sketch, "E759", {"start": v(32.45, 7.64) * mm, "end": v(33.4, 8.23) * mm});
            skLineSegment(sketch, "E760", {"start": v(33.4, 8.23) * mm, "end": v(33.67, 8.48) * mm});
            skLineSegment(sketch, "E761", {"start": v(33.67, 8.48) * mm, "end": v(33.82, 8.62) * mm});
            skLineSegment(sketch, "E762", {"start": v(33.82, 8.62) * mm, "end": v(34.27, 9.23) * mm});
            skLineSegment(sketch, "E763", {"start": v(34.27, 9.23) * mm, "end": v(34.36, 9.8) * mm});
            skLineSegment(sketch, "E764", {"start": v(34.36, 9.8) * mm, "end": v(34.33, 9.93) * mm});
            skLineSegment(sketch, "E765", {"start": v(25.58, 22.06) * mm, "end": v(26.18, 22.11) * mm});
            skLineSegment(sketch, "E766", {"start": v(26.18, 22.11) * mm, "end": v(28.68, 22.5) * mm});
            skLineSegment(sketch, "E767", {"start": v(28.68, 22.5) * mm, "end": v(30.6, 23.05) * mm});
            skLineSegment(sketch, "E768", {"start": v(30.6, 23.05) * mm, "end": v(30.9, 23.18) * mm});
            skLineSegment(sketch, "E769", {"start": v(30.9, 23.18) * mm, "end": v(30.98, 23.2) * mm});
            skLineSegment(sketch, "E770", {"start": v(30.98, 23.2) * mm, "end": v(31.33, 23.37) * mm});
            skLineSegment(sketch, "E771", {"start": v(31.33, 23.37) * mm, "end": v(31.53, 23.6) * mm});
            skLineSegment(sketch, "E772", {"start": v(31.53, 23.6) * mm, "end": v(31.53, 23.68) * mm});
            skLineSegment(sketch, "E773", {"start": v(31.53, 23.68) * mm, "end": v(31.53, 23.74) * mm});
            skLineSegment(sketch, "E774", {"start": v(31.53, 23.74) * mm, "end": v(31.4, 23.98) * mm});
            skLineSegment(sketch, "E775", {"start": v(31.4, 23.98) * mm, "end": v(31.08, 24.22) * mm});
            skLineSegment(sketch, "E776", {"start": v(31.08, 24.22) * mm, "end": v(30.98, 24.28) * mm});
            skLineSegment(sketch, "E777", {"start": v(30.98, 24.28) * mm, "end": v(30.54, 24.55) * mm});
            skLineSegment(sketch, "E778", {"start": v(30.54, 24.55) * mm, "end": v(29.16, 25.23) * mm});
            skLineSegment(sketch, "E779", {"start": v(29.16, 25.23) * mm, "end": v(26.54, 26.2) * mm});
            skLineSegment(sketch, "E780", {"start": v(26.54, 26.2) * mm, "end": v(23.07, 26.98) * mm});
            skLineSegment(sketch, "E781", {"start": v(23.07, 26.98) * mm, "end": v(19.84, 27.33) * mm});
            skLineSegment(sketch, "E782", {"start": v(19.84, 27.33) * mm, "end": v(18.76, 27.36) * mm});
            skLineSegment(sketch, "E783", {"start": v(18.76, 27.36) * mm, "end": v(18.5, 27.36) * mm});
            skLineSegment(sketch, "E784", {"start": v(18.5, 27.36) * mm, "end": v(17.31, 27.4) * mm});
            skLineSegment(sketch, "E785", {"start": v(17.31, 27.4) * mm, "end": v(13.76, 27.22) * mm});
            skLineSegment(sketch, "E786", {"start": v(13.76, 27.22) * mm, "end": v(10.29, 26.66) * mm});
            skLineSegment(sketch, "E787", {"start": v(10.29, 26.66) * mm, "end": v(7.9, 25.9) * mm});
            skLineSegment(sketch, "E788", {"start": v(7.9, 25.9) * mm, "end": v(6.76, 25.33) * mm});
            skLineSegment(sketch, "E789", {"start": v(6.76, 25.33) * mm, "end": v(6.4, 25.1) * mm});
            skLineSegment(sketch, "E790", {"start": v(6.4, 25.1) * mm, "end": v(6.3, 25.04) * mm});
            skLineSegment(sketch, "E791", {"start": v(6.3, 25.04) * mm, "end": v(6, 24.8) * mm});
            skLineSegment(sketch, "E792", {"start": v(6, 24.8) * mm, "end": v(5.9, 24.59) * mm});
            skLineSegment(sketch, "E793", {"start": v(5.9, 24.59) * mm, "end": v(5.9, 24.53) * mm});
            skLineSegment(sketch, "E794", {"start": v(5.9, 24.53) * mm, "end": v(5.9, 24.45) * mm});
            skLineSegment(sketch, "E795", {"start": v(5.9, 24.45) * mm, "end": v(6.06, 24.17) * mm});
            skLineSegment(sketch, "E796", {"start": v(6.06, 24.17) * mm, "end": v(6.39, 23.97) * mm});
            skLineSegment(sketch, "E797", {"start": v(6.39, 23.97) * mm, "end": v(6.47, 23.93) * mm});
            skLineSegment(sketch, "E798", {"start": v(6.47, 23.93) * mm, "end": v(7.26, 23.52) * mm});
            skLineSegment(sketch, "E799", {"start": v(7.26, 23.52) * mm, "end": v(9.86, 22.73) * mm});
            skLineSegment(sketch, "E800", {"start": v(9.86, 22.73) * mm, "end": v(14.34, 22) * mm});
            skLineSegment(sketch, "E801", {"start": v(14.34, 22) * mm, "end": v(19.66, 21.77) * mm});
            skLineSegment(sketch, "E802", {"start": v(19.66, 21.77) * mm, "end": v(24.1, 21.93) * mm});
            skLineSegment(sketch, "E803", {"start": v(24.1, 21.93) * mm, "end": v(25.58, 22.06) * mm});
            skLineSegment(sketch, "E804", {"start": v(19.98, 20.25) * mm, "end": v(18.7, 20.28) * mm});
            skLineSegment(sketch, "E805", {"start": v(18.7, 20.28) * mm, "end": v(14.9, 20.57) * mm});
            skLineSegment(sketch, "E806", {"start": v(14.9, 20.57) * mm, "end": v(11, 21.15) * mm});
            skLineSegment(sketch, "E807", {"start": v(11, 21.15) * mm, "end": v(8.01, 21.9) * mm});
            skLineSegment(sketch, "E808", {"start": v(8.01, 21.9) * mm, "end": v(6.3, 22.52) * mm});
            skLineSegment(sketch, "E809", {"start": v(6.3, 22.52) * mm, "end": v(5.75, 22.76) * mm});
            skLineSegment(sketch, "E810", {"start": v(5.75, 22.76) * mm, "end": v(5.43, 13.33) * mm});
            skLineSegment(sketch, "E811", {"start": v(5.43, 13.33) * mm, "end": v(5.63, 13.17) * mm});
            skLineSegment(sketch, "E812", {"start": v(5.63, 13.17) * mm, "end": v(6.3, 12.76) * mm});
            skLineSegment(sketch, "E813", {"start": v(6.3, 12.76) * mm, "end": v(7.56, 12.15) * mm});
            skLineSegment(sketch, "E814", {"start": v(7.56, 12.15) * mm, "end": v(9.25, 11.55) * mm});
            skLineSegment(sketch, "E815", {"start": v(9.25, 11.55) * mm, "end": v(11.36, 11) * mm});
            skLineSegment(sketch, "E816", {"start": v(11.36, 11) * mm, "end": v(13.92, 10.59) * mm});
            skLineSegment(sketch, "E817", {"start": v(13.92, 10.59) * mm, "end": v(16.92, 10.34) * mm});
            skLineSegment(sketch, "E818", {"start": v(16.92, 10.34) * mm, "end": v(20.38, 10.32) * mm});
            skLineSegment(sketch, "E819", {"start": v(20.38, 10.32) * mm, "end": v(23.33, 10.48) * mm});
            skLineSegment(sketch, "E820", {"start": v(23.33, 10.48) * mm, "end": v(24.31, 10.57) * mm});
            skLineSegment(sketch, "E821", {"start": v(24.31, 10.57) * mm, "end": v(24.93, 10.64) * mm});
            skLineSegment(sketch, "E822", {"start": v(24.93, 10.64) * mm, "end": v(26.78, 10.96) * mm});
            skLineSegment(sketch, "E823", {"start": v(26.78, 10.96) * mm, "end": v(28.77, 11.52) * mm});
            skLineSegment(sketch, "E824", {"start": v(28.77, 11.52) * mm, "end": v(30.3, 12.18) * mm});
            skLineSegment(sketch, "E825", {"start": v(30.3, 12.18) * mm, "end": v(31.12, 12.66) * mm});
            skLineSegment(sketch, "E826", {"start": v(31.12, 12.66) * mm, "end": v(31.36, 12.85) * mm});
            skLineSegment(sketch, "E827", {"start": v(31.36, 12.85) * mm, "end": v(31.67, 21.86) * mm});
            skLineSegment(sketch, "E828", {"start": v(31.67, 21.86) * mm, "end": v(31, 21.59) * mm});
            skLineSegment(sketch, "E829", {"start": v(31, 21.59) * mm, "end": v(28.89, 21.06) * mm});
            skLineSegment(sketch, "E830", {"start": v(28.89, 21.06) * mm, "end": v(25.72, 20.58) * mm});
            skLineSegment(sketch, "E831", {"start": v(25.72, 20.58) * mm, "end": v(22.6, 20.34) * mm});
            skLineSegment(sketch, "E832", {"start": v(22.6, 20.34) * mm, "end": v(20.64, 20.26) * mm});
            skLineSegment(sketch, "E833", {"start": v(20.64, 20.26) * mm, "end": v(19.98, 20.25) * mm});
            skCircle(sketch, "E834", {"center": v(0, 0) * mm, "radius": 55 * mm});
            skLineSegment(sketch, "E835", {"start": v(32.1, -10.6) * mm, "end": v(32.4, -10.42) * mm});
            skLineSegment(sketch, "E836", {"start": v(20.26, -12.09) * mm, "end": v(19.59, -11.28) * mm});
            skLineSegment(sketch, "E837", {"start": v(31.67, 11.43) * mm, "end": v(31.77, 11.41) * mm});
            skSolve(sketch);
        }
        {
            var Q0;
            Q0=makeQuery(id+"F0.imprint","IMPRINT",FACE,{"disambiguationData":[TD([[makeQuery(id+"F0.imprint","IMPRINT",EDGE,{"derivedFrom":sQuery(id+"F0.wireOp",EDGE,"E0")}),1.0]])]});
            extrude(context, id + "F1", {"entities" : qUnion([Q0]), "depth" : 4 * mm});
        }
        {
            var Q0;
            Q0=makeQuery(id+"F0.imprint","IMPRINT",FACE,{"disambiguationData":[TD([[makeQuery(id+"F0.imprint","IMPRINT",EDGE,{"derivedFrom":sQuery(id+"F0.wireOp",EDGE,"E419")}),-1.0]])]});
            extrude(context, id + "F2", {"entities" : qUnion([Q0]), "operationType" : NewBodyOperationType.ADD, "depth" : 5 * mm});
        }
        {
            var Q0;
            Q0=makeQuery(id+"F0.imprint","IMPRINT",FACE,{"disambiguationData":[TD([[makeQuery(id+"F0.imprint","IMPRINT",EDGE,{"derivedFrom":sQuery(id+"F0.wireOp",EDGE,"E804")}),1.0]])]});
            var Q1;
            Q1=makeQuery(id+"F0.imprint","IMPRINT",FACE,{"disambiguationData":[TD([[makeQuery(id+"F0.imprint","IMPRINT",EDGE,{"derivedFrom":sQuery(id+"F0.wireOp",EDGE,"E709")}),1.0]])]});
            var Q2;
            Q2=makeQuery(id+"F0.imprint","IMPRINT",FACE,{"disambiguationData":[TD([[makeQuery(id+"F0.imprint","IMPRINT",EDGE,{"derivedFrom":sQuery(id+"F0.wireOp",EDGE,"E765")}),1.0]])]});
            extrude(context, id + "F3", {"entities" : qUnion([Q0, Q1, Q2]), "operationType" : NewBodyOperationType.ADD, "depth" : 5 * mm});
        }
        {
            var Q0;
            Q0=makeQuery(id+"F0.imprint","IMPRINT",FACE,{"disambiguationData":[TD([[makeQuery(id+"F0.imprint","IMPRINT",EDGE,{"derivedFrom":sQuery(id+"F0.wireOp",EDGE,"E0")}),-1.0]])]});
            extrude(context, id + "F4", {"entities" : qUnion([Q0]), "operationType" : NewBodyOperationType.ADD, "depth" : 3.5 * mm});
        }
        {
            var Q0;
            Q0=makeQuery(id+"F0.imprint","IMPRINT",FACE,{"disambiguationData":[TD([[makeQuery(id+"F0.imprint","IMPRINT",EDGE,{"derivedFrom":sQuery(id+"F0.wireOp",EDGE,"E648")}),-1.0]])]});
            var Q1;
            Q1=makeQuery(id+"F0.imprint","IMPRINT",FACE,{"disambiguationData":[TD([[makeQuery(id+"F0.imprint","IMPRINT",EDGE,{"derivedFrom":sQuery(id+"F0.wireOp",EDGE,"E679")}),-1.0]])]});
            extrude(context, id + "F5", {"entities" : qUnion([Q0, Q1]), "operationType" : NewBodyOperationType.ADD, "depth" : 3 * mm});
        }
        {
            var Q0;
            Q0=makeQuery(id+"F0.imprint","IMPRINT",FACE,{"disambiguationData":[TD([[makeQuery(id+"F0.imprint","IMPRINT",EDGE,{"derivedFrom":sQuery(id+"F0.wireOp",EDGE,"E532")}),1.0]])]});
            extrude(context, id + "F6", {"entities" : qUnion([Q0]), "operationType" : NewBodyOperationType.ADD, "depth" : 3.5 * mm});
        }
    });
